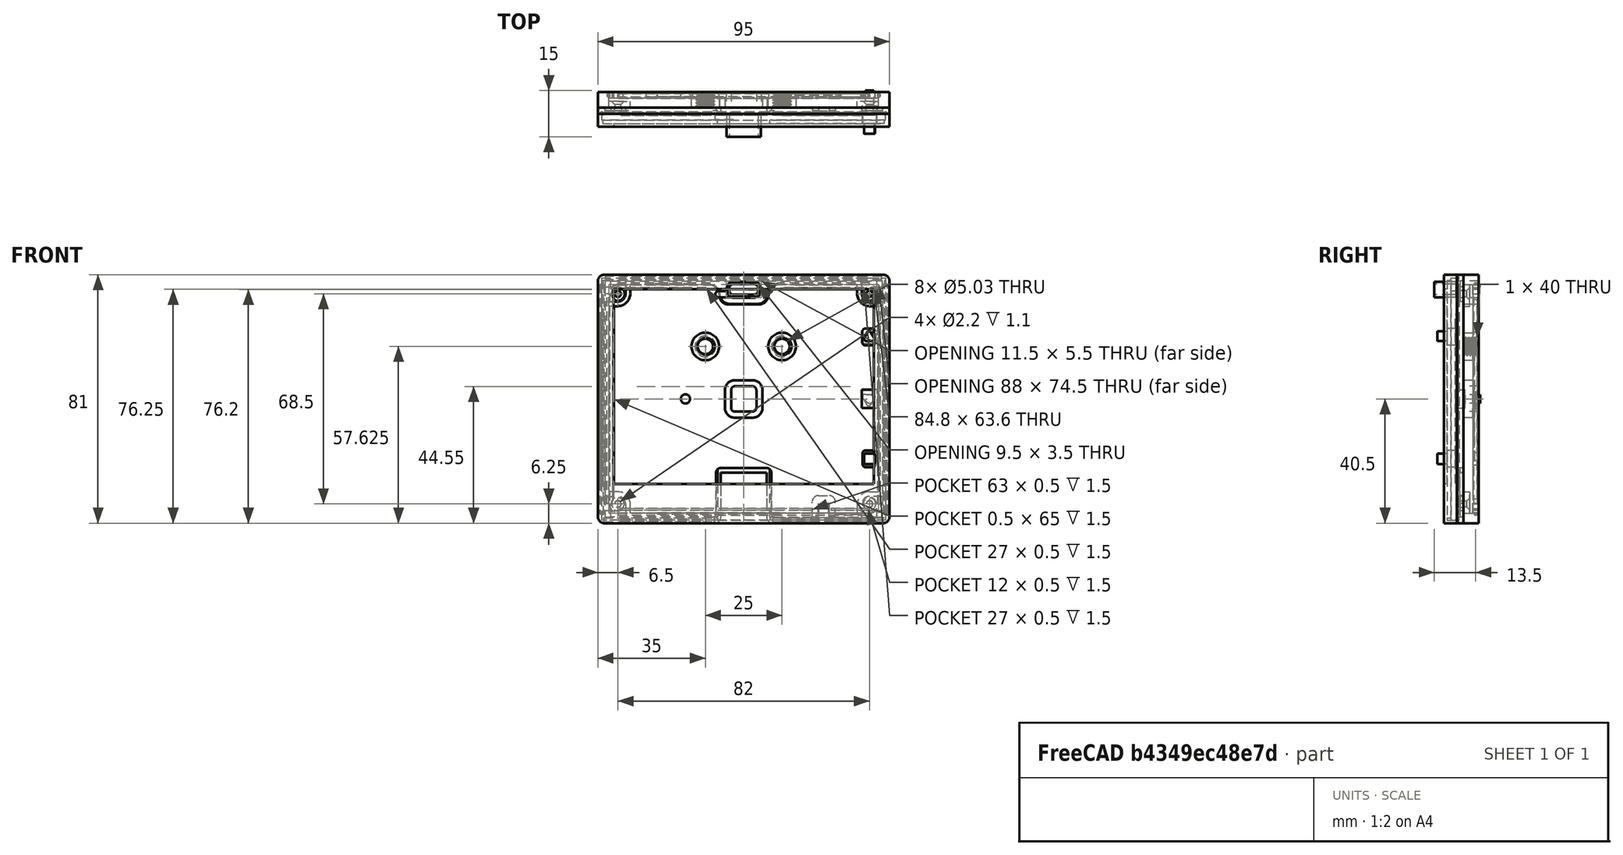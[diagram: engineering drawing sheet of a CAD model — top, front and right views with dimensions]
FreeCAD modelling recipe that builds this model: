
FCSTD DOCUMENT  (FreeCAD 1.1RUnknown)
Label: Altruist_Insight
License: All rights reserved
LicenseURL: http://en.wikipedia.org/wiki/All_rights_reserved
objects: Sketcher::SketchObject×26, PartDesign::Pad×18, PartDesign::Body×8, App::Point×8, PartDesign::Groove×7, PartDesign::Revolution×6, PartDesign::Pocket×4, PartDesign::Mirrored×3, PartDesign::Chamfer×1, Mesh::Feature×1, PartDesign::Hole×1
note: 177 computed .brp shape members not serialized (recipe doc carries the construction recipe); baked Part::Feature solids carry a one-line shape summary decoded from their .brp

FEATURE [Sketcher::SketchObject] Sketch004
  ArcFitTolerance = 1e-06
  AttachmentSupport = -> [XZ_Plane003]
  ExternalTypes = [0]
  FullyConstrained = true
  MakeInternals = false
  MapMode = 5
  Placement = pos=(0,0,0) rot=(1,0,0;1.5708rad)
  _ExternalGeoVersion = 0
  sketch-geometry (14):
    g0: LineSegment StartX=-42.4 StartY=-27.75 StartZ=0 EndX=42.4 EndY=-27.75 EndZ=0
    g1: LineSegment StartX=42.4 StartY=-27.75 StartZ=0 EndX=42.4 EndY=35.85 EndZ=0
    g2: LineSegment StartX=42.4 StartY=35.85 StartZ=0 EndX=-42.4 EndY=35.85 EndZ=0
    g3: LineSegment StartX=-42.4 StartY=35.85 StartZ=0 EndX=-42.4 EndY=-27.75 EndZ=0
    g4: LineSegment StartX=-47.5 StartY=38.5 StartZ=0 EndX=-47.5 EndY=-38.5 EndZ=0
    g5: LineSegment StartX=-45.5 StartY=-40.5 StartZ=0 EndX=45.5 EndY=-40.5 EndZ=0
    g6: LineSegment StartX=47.5 StartY=-38.5 StartZ=0 EndX=47.5 EndY=38.5 EndZ=0
    g7: LineSegment StartX=45.5 StartY=40.5 StartZ=0 EndX=-45.5 EndY=40.5 EndZ=0
    g8: ArcOfCircle CenterX=-45.5 CenterY=38.5 CenterZ=0 NormalX=0 NormalY=0 NormalZ=1 AngleXU=0 Radius=2 StartAngle=1.5708 EndAngle=3.14159
    g9: ArcOfCircle CenterX=-45.5 CenterY=-38.5 CenterZ=0 NormalX=0 NormalY=0 NormalZ=1 AngleXU=0 Radius=2 StartAngle=3.14159 EndAngle=4.71239
    g10: ArcOfCircle CenterX=45.5 CenterY=-38.5 CenterZ=0 NormalX=0 NormalY=0 NormalZ=1 AngleXU=0 Radius=2 StartAngle=4.71239 EndAngle=6.28319
    g11: ArcOfCircle CenterX=45.5 CenterY=38.5 CenterZ=0 NormalX=0 NormalY=0 NormalZ=1 AngleXU=0 Radius=2 StartAngle=-1.8e-15 EndAngle=1.5708
    g12: GeomPoint [constr] X=-47.5 Y=40.5 Z=0
    g13: GeomPoint [constr] X=47.5 Y=-40.5 Z=0
  constraints (34):
    c: Coincident(g0,g1)
    c: Coincident(g1,g2)
    c: Coincident(g2,g3)
    c: Coincident(g3,g0)
    c: Horizontal(g0)
    c: Vertical(g1)
    c: Vertical(g3)
    c: Distance(g1,g3) = 84.8
    c: Distance(g0,g2) = 63.6
    c: Tangent(g4,g8) = -1.5708
    c: Tangent(g4,g9) = -1.5708
    c: Tangent(g5,g9) = -1.5708
    c: Tangent(g5,g10) = -1.5708
    c: Tangent(g6,g10) = -1.5708
    c: Tangent(g6,g11) = -1.5708
    c: Tangent(g7,g11) = -1.5708
    c: Tangent(g7,g8) = -1.5708
    c: Vertical(g4)
    c: Vertical(g6)
    c: Horizontal(g5)
    c: Horizontal(g7)
    c: Equal(g8,g9)
    c: Equal(g9,g10)
    c: Equal(g10,g11)
    c: PointOnObject(g12,g4)
    c: PointOnObject(g12,g7)
    c: PointOnObject(g13,g5)
    c: PointOnObject(g13,g6)
    c: Radius(g9) = 2
    c: Distance(g6,g4) = 95
    c: Distance(g5,g7) = 81
    c: Symmetric(g12,g13,g-1)
    c: Symmetric(g2,g1,g-2)
    c: Distance(g2,g7) = 4.65
FEATURE [PartDesign::Pad] Pad004
  Direction = (0,-1,2e-16)
  Length = 1
  Length2 = 10
  Placement = pos=(0,0,0) rot=(1,0,0;1.5708rad)
  Profile = -> Sketch004
  ReferenceAxis = -> Sketch004 [N_Axis]
  SideType = 0
  Suppressed = false
  Type = 0
  Type2 = 0
FEATURE [Sketcher::SketchObject] Sketch005
  ArcFitTolerance = 1e-06
  AttachmentSupport = -> [Pad004]
  ExternalGeometry = -> [Sketch004]
  ExternalTypes = [0]
  FullyConstrained = true
  MakeInternals = false
  MapMode = 5
  Placement = pos=(0,4e-16,0) rot=(-1,0,0;1.5708rad)
  _ExternalGeoVersion = 0
  sketch-geometry (18):
    g0: LineSegment StartX=45.875 StartY=-38.75 StartZ=0 EndX=45.875 EndY=38.75 EndZ=0
    g1: LineSegment StartX=-45.875 StartY=-38.75 StartZ=0 EndX=-45.875 EndY=38.75 EndZ=0
    g2: LineSegment StartX=-45.875 StartY=38.75 StartZ=0 EndX=-8.5 EndY=38.75 EndZ=0
    g3: LineSegment StartX=45.875 StartY=38.75 StartZ=0 EndX=8.5 EndY=38.75 EndZ=0
    g4: LineSegment StartX=8.5 StartY=38.75 StartZ=0 EndX=8.5 EndY=39.5 EndZ=0
    g5: LineSegment StartX=-8.5 StartY=38.75 StartZ=0 EndX=-8.5 EndY=39.5 EndZ=0
    g6: LineSegment StartX=-8.5 StartY=39.5 StartZ=0 EndX=8.5 EndY=39.5 EndZ=0
    g7: LineSegment StartX=-45.875 StartY=-38.75 StartZ=0 EndX=45.875 EndY=-38.75 EndZ=0
    g8: LineSegment StartX=-47.5 StartY=38.5 StartZ=0 EndX=-47.5 EndY=-38.5 EndZ=0
    g9: LineSegment StartX=-45.5 StartY=-40.5 StartZ=0 EndX=45.5 EndY=-40.5 EndZ=0
    g10: LineSegment StartX=47.5 StartY=-38.5 StartZ=0 EndX=47.5 EndY=38.5 EndZ=0
    g11: LineSegment StartX=45.5 StartY=40.5 StartZ=0 EndX=-45.5 EndY=40.5 EndZ=0
    g12: ArcOfCircle CenterX=-45.5 CenterY=38.5 CenterZ=0 NormalX=0 NormalY=0 NormalZ=1 AngleXU=0 Radius=2 StartAngle=1.5708 EndAngle=3.14159
    g13: ArcOfCircle CenterX=-45.5 CenterY=-38.5 CenterZ=0 NormalX=0 NormalY=0 NormalZ=1 AngleXU=0 Radius=2 StartAngle=3.14159 EndAngle=4.71239
    g14: ArcOfCircle CenterX=45.5 CenterY=-38.5 CenterZ=0 NormalX=0 NormalY=0 NormalZ=1 AngleXU=0 Radius=2 StartAngle=4.71239 EndAngle=6.28319
    g15: ArcOfCircle CenterX=45.5 CenterY=38.5 CenterZ=0 NormalX=0 NormalY=0 NormalZ=1 AngleXU=0 Radius=2 StartAngle=1.3e-15 EndAngle=1.5708
    g16: GeomPoint [constr] X=-47.5 Y=40.5 Z=0
    g17: GeomPoint [constr] X=47.5 Y=-40.5 Z=0
  constraints (44):
    c: Vertical(g0)
    c: Vertical(g1)
    c: DistanceX(g1,g0) = 91.75
    c: DistanceY(g1,g1) = 77.5
    c: Symmetric(g0,g1,g-1)
    c: Coincident(g2,g1)
    c: Horizontal(g2)
    c: Coincident(g3,g0)
    c: Horizontal(g3)
    c: Coincident(g4,g3)
    c: Vertical(g4)
    c: Coincident(g5,g2)
    c: Vertical(g5)
    c: Coincident(g6,g5)
    c: Coincident(g6,g4)
    c: Symmetric(g5,g4,g-2)
    c: Equal(g0,g1)
    c: DistanceX(g6,g6) = 17
    c: Coincident(g7,g1)
    c: Coincident(g7,g0)
    c: Horizontal(g7)
    c: Distance(g4,g4) = 0.75
    c: Tangent(g8,g12) = -1.5708
    c: Tangent(g8,g13) = -1.5708
    c: Tangent(g9,g13) = -1.5708
    c: Tangent(g9,g14) = -1.5708
    c: Tangent(g10,g14) = -1.5708
    c: Tangent(g10,g15) = -1.5708
    c: Tangent(g11,g15) = -1.5708
    c: Tangent(g11,g12) = -1.5708
    c: Vertical(g8)
    c: Vertical(g10)
    c: Horizontal(g9)
    c: Horizontal(g11)
    c: Equal(g12,g13)
    c: Equal(g13,g14)
    c: Equal(g14,g15)
    c: PointOnObject(g16,g8)
    c: PointOnObject(g16,g11)
    c: PointOnObject(g17,g9)
    c: PointOnObject(g17,g10)
    c: Radius(g13) = 2
    c: Symmetric(g15,g13,g-1)
    c: Coincident(g-3,g11)
FEATURE [PartDesign::Pad] Pad005
  BaseFeature = -> Pad004
  Direction = (0,1,2e-16)
  Length = 1.2
  Length2 = 10
  Placement = pos=(0,0,0) rot=(1,0,0;1.5708rad)
  Profile = -> Sketch005
  ReferenceAxis = -> Sketch005 [N_Axis]
  Refine = true
  SideType = 0
  Suppressed = false
  Type = 0
  Type2 = 0
FEATURE [Sketcher::SketchObject] Sketch006
  ArcFitTolerance = 1e-06
  AttachmentSupport = -> [Pad005]
  ExternalGeometry = -> [Pad005]
  ExternalTypes = [0]
  FullyConstrained = true
  MakeInternals = false
  MapMode = 5
  Placement = pos=(0,1.2,0) rot=(-1,0,0;1.5708rad)
  _ExternalGeoVersion = 0
  sketch-geometry (14):
    g0: LineSegment StartX=-46.25 StartY=39.5 StartZ=0 EndX=-46.25 EndY=-39.5 EndZ=0
    g1: LineSegment StartX=-46.25 StartY=-39.5 StartZ=0 EndX=46.25 EndY=-39.5 EndZ=0
    g2: LineSegment StartX=46.25 StartY=-39.5 StartZ=0 EndX=46.25 EndY=39.5 EndZ=0
    g3: LineSegment StartX=46.25 StartY=39.5 StartZ=0 EndX=-46.25 EndY=39.5 EndZ=0
    g4: LineSegment StartX=-47.5 StartY=38.5 StartZ=0 EndX=-47.5 EndY=-38.5 EndZ=0
    g5: LineSegment StartX=-45.5 StartY=-40.5 StartZ=0 EndX=45.5 EndY=-40.5 EndZ=0
    g6: LineSegment StartX=47.5 StartY=-38.5 StartZ=0 EndX=47.5 EndY=38.5 EndZ=0
    g7: LineSegment StartX=45.5 StartY=40.5 StartZ=0 EndX=-45.5 EndY=40.5 EndZ=0
    g8: ArcOfCircle CenterX=-45.5 CenterY=38.5 CenterZ=0 NormalX=0 NormalY=0 NormalZ=1 AngleXU=0 Radius=2 StartAngle=1.5708 EndAngle=3.14159
    g9: ArcOfCircle CenterX=-45.5 CenterY=-38.5 CenterZ=0 NormalX=0 NormalY=0 NormalZ=1 AngleXU=0 Radius=2 StartAngle=3.14159 EndAngle=4.71239
    g10: ArcOfCircle CenterX=45.5 CenterY=-38.5 CenterZ=0 NormalX=0 NormalY=0 NormalZ=1 AngleXU=0 Radius=2 StartAngle=4.71239 EndAngle=6.28319
    g11: ArcOfCircle CenterX=45.5 CenterY=38.5 CenterZ=0 NormalX=0 NormalY=0 NormalZ=1 AngleXU=0 Radius=2 StartAngle=1.6e-15 EndAngle=1.5708
    g12: GeomPoint [constr] X=-47.5 Y=40.5 Z=0
    g13: GeomPoint [constr] X=47.5 Y=-40.5 Z=0
  constraints (33):
    c: Coincident(g0,g1)
    c: Coincident(g1,g2)
    c: Coincident(g2,g3)
    c: Coincident(g3,g0)
    c: Vertical(g0)
    c: Vertical(g2)
    c: Horizontal(g1)
    c: Horizontal(g3)
    c: DistanceY(g2,g2) = 79
    c: DistanceX(g3,g3) = 92.5
    c: Symmetric(g0,g2,g-1)
    c: Tangent(g4,g8) = -1.5708
    c: Tangent(g4,g9) = -1.5708
    c: Tangent(g5,g9) = -1.5708
    c: Tangent(g5,g10) = -1.5708
    c: Tangent(g6,g10) = -1.5708
    c: Tangent(g6,g11) = -1.5708
    c: Tangent(g7,g11) = -1.5708
    c: Tangent(g7,g8) = -1.5708
    c: Vertical(g4)
    c: Vertical(g6)
    c: Horizontal(g5)
    c: Horizontal(g7)
    c: Equal(g8,g9)
    c: Equal(g9,g10)
    c: Equal(g10,g11)
    c: PointOnObject(g12,g4)
    c: PointOnObject(g12,g7)
    c: PointOnObject(g13,g5)
    c: PointOnObject(g13,g6)
    c: Radius(g9) = 2
    c: Symmetric(g11,g9,g-1)
    c: Coincident(g-3,g7)
FEATURE [PartDesign::Pad] Pad006
  BaseFeature = -> Pad005
  Direction = (0,1,2e-16)
  Length = 2
  Length2 = 10
  Placement = pos=(0,0,0) rot=(1,0,0;1.5708rad)
  Profile = -> Sketch006
  ReferenceAxis = -> Sketch006 [N_Axis]
  Refine = true
  SideType = 0
  Suppressed = false
  Type = 0
  Type2 = 0
FEATURE [Sketcher::SketchObject] Sketch007
  ArcFitTolerance = 1e-06
  AttachmentSupport = -> [Pad006]
  ExternalTypes = [0]
  FullyConstrained = true
  MakeInternals = false
  MapMode = 5
  Placement = pos=(0,0,39.5) rot=(1,0,0;3.14159rad)
  _ExternalGeoVersion = 0
  sketch-geometry (4):
    g0: LineSegment StartX=40 StartY=-3.2 StartZ=0 EndX=40 EndY=-2.7 EndZ=0
    g1: LineSegment StartX=40 StartY=-2.7 StartZ=0 EndX=-40 EndY=-2.7 EndZ=0
    g2: LineSegment StartX=-40 StartY=-2.7 StartZ=0 EndX=-40 EndY=-3.2 EndZ=0
    g3: LineSegment StartX=-40 StartY=-3.2 StartZ=0 EndX=40 EndY=-3.2 EndZ=0
  constraints (11):
    c: Coincident(g0,g1)
    c: Coincident(g1,g2)
    c: Coincident(g2,g3)
    c: Coincident(g3,g0)
    c: Vertical(g0)
    c: Vertical(g2)
    c: DistanceY(g2,g2) = 0.5
    c: Symmetric(g1,g0,g-2)
    c: DistanceX(g1,g1) = 80
    c: Distance(g-1,g3) = 3.2
    c: Horizontal(g3)
FEATURE [PartDesign::Revolution] Revolution
  Angle = 360
  Angle2 = 60
  Axis = (1,0,0)
  Base = (-46.25,3.2,39.5)
  BaseFeature = -> Pad006
  FuseOrder = 1
  Placement = pos=(0,0,0) rot=(1,0,0;1.5708rad)
  Profile = -> Sketch007
  ReferenceAxis = -> Pad006 [Edge26]
  Refine = true
  Suppressed = false
  Type = 0
FEATURE [Sketcher::SketchObject] Sketch008
  ArcFitTolerance = 1e-06
  AttachmentSupport = -> [Revolution]
  ExternalTypes = [0]
  FullyConstrained = true
  MakeInternals = false
  MapMode = 5
  Placement = pos=(46.25,0,0) rot=(0.707107,0,-0.707107;3.14159rad)
  _ExternalGeoVersion = 0
  sketch-geometry (4):
    g0: LineSegment StartX=-27.5 StartY=-2.7 StartZ=0 EndX=-27.5 EndY=-3.2 EndZ=0
    g1: LineSegment StartX=-27.5 StartY=-3.2 StartZ=0 EndX=27.5 EndY=-3.2 EndZ=0
    g2: LineSegment StartX=27.5 StartY=-3.2 StartZ=0 EndX=27.5 EndY=-2.7 EndZ=0
    g3: LineSegment StartX=27.5 StartY=-2.7 StartZ=0 EndX=-27.5 EndY=-2.7 EndZ=0
  constraints (11):
    c: Coincident(g0,g1)
    c: Coincident(g1,g2)
    c: Coincident(g2,g3)
    c: Coincident(g3,g0)
    c: Vertical(g0)
    c: Vertical(g2)
    c: Horizontal(g1)
    c: Horizontal(g0,g-3)
    c: Equal(g0,g-3)
    c: Symmetric(g2,g0,g-2)
    c: DistanceX(g3,g3) = 55
FEATURE [PartDesign::Revolution] Revolution001
  Angle = 360
  Angle2 = 60
  Axis = (0,2e-16,-1)
  Base = (46.25,3.2,39.5)
  BaseFeature = -> Revolution
  FuseOrder = 1
  Placement = pos=(0,0,0) rot=(1,0,0;1.5708rad)
  Profile = -> Sketch008
  ReferenceAxis = -> Revolution [Edge19]
  Refine = true
  Reversed = true
  Suppressed = false
  Type = 0
FEATURE [Sketcher::SketchObject] Sketch011
  ArcFitTolerance = 1e-06
  AttachmentSupport = -> [XZ_Plane004]
  ExternalTypes = [0]
  FullyConstrained = true
  MakeInternals = false
  MapMode = 5
  Placement = pos=(0,0,0) rot=(1,0,0;1.5708rad)
  _ExternalGeoVersion = 0
  sketch-geometry (58):
    g0: LineSegment StartX=-47.5 StartY=38.5 StartZ=0 EndX=-47.5 EndY=-38.5 EndZ=0
    g1: LineSegment StartX=-45.5 StartY=-40.5 StartZ=0 EndX=45.5 EndY=-40.5 EndZ=0
    g2: LineSegment StartX=47.5 StartY=-38.5 StartZ=0 EndX=47.5 EndY=38.5 EndZ=0
    g3: LineSegment StartX=45.5 StartY=40.5 StartZ=0 EndX=-45.5 EndY=40.5 EndZ=0
    g4: ArcOfCircle CenterX=-45.5 CenterY=38.5 CenterZ=0 NormalX=0 NormalY=0 NormalZ=1 AngleXU=0 Radius=2 StartAngle=1.5708 EndAngle=3.14159
    g5: ArcOfCircle CenterX=-45.5 CenterY=-38.5 CenterZ=0 NormalX=0 NormalY=0 NormalZ=1 AngleXU=0 Radius=2 StartAngle=3.14159 EndAngle=4.71239
    g6: ArcOfCircle CenterX=45.5 CenterY=-38.5 CenterZ=0 NormalX=0 NormalY=0 NormalZ=1 AngleXU=0 Radius=2 StartAngle=4.71239 EndAngle=6.28319
    g7: ArcOfCircle CenterX=45.5 CenterY=38.5 CenterZ=0 NormalX=0 NormalY=0 NormalZ=1 AngleXU=0 Radius=2 StartAngle=1e-16 EndAngle=1.5708
    g8: GeomPoint [constr] X=-47.5 Y=40.5 Z=0
    g9: GeomPoint [constr] X=47.5 Y=-40.5 Z=0
    g10: LineSegment StartX=-4.75 StartY=36 StartZ=0 EndX=-4.75 EndY=35.5 EndZ=0
    g11: LineSegment StartX=-3.25 StartY=34 StartZ=0 EndX=3.25 EndY=34 EndZ=0
    g12: LineSegment StartX=4.75 StartY=35.5 StartZ=0 EndX=4.75 EndY=36 EndZ=0
    g13: LineSegment StartX=3.25 StartY=37.5 StartZ=0 EndX=-3.25 EndY=37.5 EndZ=0
    g14: ArcOfCircle CenterX=-3.25 CenterY=36 CenterZ=0 NormalX=0 NormalY=0 NormalZ=1 AngleXU=0 Radius=1.5 StartAngle=1.5708 EndAngle=3.14159
    g15: ArcOfCircle CenterX=-3.25 CenterY=35.5 CenterZ=0 NormalX=0 NormalY=0 NormalZ=1 AngleXU=0 Radius=1.5 StartAngle=3.14159 EndAngle=4.71239
    g16: ArcOfCircle CenterX=3.25 CenterY=35.5 CenterZ=0 NormalX=0 NormalY=0 NormalZ=1 AngleXU=0 Radius=1.5 StartAngle=4.71239 EndAngle=6.28319
    g17: ArcOfCircle CenterX=3.25 CenterY=36 CenterZ=0 NormalX=0 NormalY=0 NormalZ=1 AngleXU=0 Radius=1.5 StartAngle=3e-16 EndAngle=1.5708
    g18: GeomPoint [constr] X=-4.75 Y=37.5 Z=0
    g19: GeomPoint [constr] X=4.75 Y=34 Z=0
    g20: Circle CenterX=41 CenterY=34.25 CenterZ=0 NormalX=0 NormalY=0 NormalZ=1 AngleXU=0 Radius=1
    g21: Circle CenterX=-41 CenterY=34.25 CenterZ=0 NormalX=0 NormalY=0 NormalZ=1 AngleXU=0 Radius=1
    g22: Circle CenterX=-41 CenterY=-34.25 CenterZ=0 NormalX=0 NormalY=0 NormalZ=1 AngleXU=0 Radius=1
    g23: Circle CenterX=41 CenterY=-34.25 CenterZ=0 NormalX=0 NormalY=0 NormalZ=1 AngleXU=0 Radius=1
    g24: ArcOfCircle CenterX=41 CenterY=34.25 CenterZ=0 NormalX=0 NormalY=0 NormalZ=1 AngleXU=0 Radius=3 StartAngle=1e-15 EndAngle=1.5708
    g25: ArcOfCircle CenterX=41 CenterY=-34.25 CenterZ=0 NormalX=0 NormalY=0 NormalZ=1 AngleXU=0 Radius=3 StartAngle=4.71239 EndAngle=6.28319
    g26: ArcOfCircle CenterX=-41 CenterY=-34.25 CenterZ=0 NormalX=0 NormalY=0 NormalZ=1 AngleXU=0 Radius=3 StartAngle=3.14159 EndAngle=4.71239
    g27: ArcOfCircle CenterX=-41 CenterY=-34.25 CenterZ=0 NormalX=0 NormalY=0 NormalZ=1 AngleXU=0 Radius=4 StartAngle=0 EndAngle=1.5708
    g28: ArcOfCircle CenterX=41 CenterY=-34.25 CenterZ=0 NormalX=0 NormalY=0 NormalZ=1 AngleXU=0 Radius=4 StartAngle=1.5708 EndAngle=3.14159
    g29: ArcOfCircle CenterX=41 CenterY=34.25 CenterZ=0 NormalX=0 NormalY=0 NormalZ=1 AngleXU=0 Radius=4 StartAngle=3.14159 EndAngle=4.71239
    g30: ArcOfCircle CenterX=-41 CenterY=34.25 CenterZ=0 NormalX=0 NormalY=0 NormalZ=1 AngleXU=0 Radius=4 StartAngle=4.71239 EndAngle=6.28319
    g31: ArcOfCircle CenterX=-41 CenterY=34.25 CenterZ=0 NormalX=0 NormalY=0 NormalZ=1 AngleXU=0 Radius=3 StartAngle=1.5708 EndAngle=3.14159
    g32: LineSegment StartX=-41 StartY=30.25 StartZ=0 EndX=-44 EndY=30.25 EndZ=0
    g33: LineSegment StartX=-37 StartY=34.25 StartZ=0 EndX=-37 EndY=37.25 EndZ=0
    g34: LineSegment StartX=-41 StartY=37.25 StartZ=0 EndX=-37 EndY=37.25 EndZ=0
    g35: LineSegment StartX=-44 StartY=30.25 StartZ=0 EndX=-44 EndY=34.25 EndZ=0
    g36: LineSegment StartX=-41 StartY=-30.25 StartZ=0 EndX=-44 EndY=-30.25 EndZ=0
    g37: LineSegment StartX=-44 StartY=-30.25 StartZ=0 EndX=-44 EndY=-34.25 EndZ=0
    g38: LineSegment StartX=-41 StartY=-37.25 StartZ=0 EndX=-37 EndY=-37.25 EndZ=0
    g39: LineSegment StartX=-37 StartY=-37.25 StartZ=0 EndX=-37 EndY=-34.25 EndZ=0
    g40: LineSegment StartX=-44 StartY=30.25 StartZ=0 EndX=-44 EndY=-30.25 EndZ=0
    g41: LineSegment StartX=41 StartY=-30.25 StartZ=0 EndX=44 EndY=-30.25 EndZ=0
    g42: LineSegment StartX=44 StartY=-34.25 StartZ=0 EndX=44 EndY=-30.25 EndZ=0
    g43: LineSegment StartX=37 StartY=-34.25 StartZ=0 EndX=37 EndY=-37.25 EndZ=0
    g44: LineSegment StartX=41 StartY=-37.25 StartZ=0 EndX=37 EndY=-37.25 EndZ=0
    g45: LineSegment StartX=-37 StartY=-37.25 StartZ=0 EndX=37 EndY=-37.25 EndZ=0
    g46: LineSegment StartX=44 StartY=34.25 StartZ=0 EndX=44 EndY=30.25 EndZ=0
    g47: LineSegment StartX=37 StartY=34.25 StartZ=0 EndX=37 EndY=37.25 EndZ=0
    g48: LineSegment StartX=37 StartY=37.25 StartZ=0 EndX=41 EndY=37.25 EndZ=0
    g49: LineSegment StartX=41 StartY=30.25 StartZ=0 EndX=44 EndY=30.25 EndZ=0
    g50: LineSegment StartX=44 StartY=-30.25 StartZ=0 EndX=44 EndY=30.25 EndZ=0
    g51: LineSegment StartX=-37 StartY=37.25 StartZ=0 EndX=-10.875 EndY=37.25 EndZ=0
    g52: LineSegment StartX=37 StartY=37.25 StartZ=0 EndX=10.875 EndY=37.25 EndZ=0
    g53: ArcOfCircle CenterX=10.875 CenterY=34.125 CenterZ=0 NormalX=0 NormalY=0 NormalZ=1 AngleXU=0 Radius=3.125 StartAngle=1.5708 EndAngle=3.14159
    g54: ArcOfCircle CenterX=-10.875 CenterY=34.125 CenterZ=0 NormalX=0 NormalY=0 NormalZ=1 AngleXU=0 Radius=3.125 StartAngle=0 EndAngle=1.5708
    g55: ArcOfCircle CenterX=-4.625 CenterY=34.125 CenterZ=0 NormalX=0 NormalY=0 NormalZ=1 AngleXU=0 Radius=3.125 StartAngle=3.14159 EndAngle=4.71239
    g56: ArcOfCircle CenterX=4.625 CenterY=34.125 CenterZ=0 NormalX=0 NormalY=0 NormalZ=1 AngleXU=0 Radius=3.125 StartAngle=4.71239 EndAngle=6.28319
    g57: LineSegment StartX=-4.625 StartY=31 StartZ=0 EndX=4.625 EndY=31 EndZ=0
  constraints (158):
    c: Tangent(g0,g4) = -1.5708
    c: Tangent(g0,g5) = -1.5708
    c: Tangent(g1,g5) = -1.5708
    c: Tangent(g1,g6) = -1.5708
    c: Tangent(g2,g6) = -1.5708
    c: Tangent(g2,g7) = -1.5708
    c: Tangent(g3,g7) = -1.5708
    c: Tangent(g3,g4) = -1.5708
    c: Vertical(g0)
    c: Vertical(g2)
    c: Horizontal(g1)
    c: Horizontal(g3)
    c: Equal(g4,g5)
    c: Equal(g5,g6)
    c: Equal(g6,g7)
    c: PointOnObject(g8,g0)
    c: PointOnObject(g8,g3)
    c: PointOnObject(g9,g1)
    c: PointOnObject(g9,g2)
    c: Distance(g2,g0) = 95
    c: Distance(g1,g3) = 81
    c: Symmetric(g8,g9,g-1)
    c: Tangent(g10,g14) = -1.5708
    c: Tangent(g10,g15) = -1.5708
    c: Tangent(g11,g15) = -1.5708
    c: Tangent(g11,g16) = -1.5708
    c: Tangent(g12,g16) = -1.5708
    c: Tangent(g12,g17) = -1.5708
    c: Tangent(g13,g17) = -1.5708
    c: Tangent(g13,g14) = -1.5708
    c: Vertical(g10)
    c: Vertical(g12)
    c: Horizontal(g11)
    c: Equal(g14,g15)
    c: Equal(g15,g16)
    c: Equal(g16,g17)
    c: PointOnObject(g18,g10)
    c: PointOnObject(g18,g13)
    c: PointOnObject(g19,g11)
    c: PointOnObject(g19,g12)
    c: Radius(g15) = 1.5
    c: Distance(g12,g10) = 9.5
    c: Distance(g11,g13) = 3.5
    c: Symmetric(g13,g13,g-2)
    c: Distance(g-1,g11) = 34
    c: Diameter(g20) = 2
    c: Diameter(g21) = 2
    c: Diameter(g22) = 2
    c: Diameter(g23) = 2
    c: Horizontal(g23,g22)
    c: Horizontal(g20,g21)
    c: Vertical(g20,g23)
    c: Vertical(g21,g22)
    c: Symmetric(g22,g20,g-1)
    c: DistanceX(g21,g20) = 82
    c: Distance(g23,g20) = 68.5
    c: Coincident(g24,g20)
    c: Coincident(g25,g23)
    c: Radius(g26) = 3
    c: Coincident(g26,g22)
    c: Coincident(g27,g22)
    c: Coincident(g28,g23)
    c: Coincident(g29,g20)
    c: Radius(g30) = 4
    c: Coincident(g30,g21)
    c: Equal(g27,g28)
    c: Equal(g28,g29)
    c: Equal(g29,g30)
    c: Coincident(g31,g21)
    c: Equal(g31,g26)
    c: Equal(g26,g25)
    c: Equal(g25,g24)
    c: Coincident(g32,g30)
    c: Horizontal(g32)
    c: Coincident(g33,g30)
    c: Vertical(g33)
    c: Coincident(g34,g31)
    c: Coincident(g34,g33)
    c: Horizontal(g34)
    c: Coincident(g35,g32)
    c: Coincident(g35,g31)
    c: Coincident(g36,g27)
    c: Horizontal(g36)
    c: Coincident(g37,g36)
    c: Coincident(g37,g26)
    c: Coincident(g38,g26)
    c: Coincident(g39,g38)
    c: Coincident(g39,g27)
    c: Vertical(g39)
    c: Coincident(g40,g32)
    c: Coincident(g40,g36)
    c: Vertical(g40)
    c: Coincident(g41,g28)
    c: Horizontal(g41)
    c: Coincident(g42,g25)
    c: Coincident(g42,g41)
    c: Coincident(g43,g28)
    c: Vertical(g43)
    c: Coincident(g44,g25)
    c: Coincident(g44,g43)
    c: Coincident(g45,g38)
    c: Coincident(g45,g43)
    c: Horizontal(g45)
    c: Coincident(g46,g24)
    c: Vertical(g46)
    c: Coincident(g47,g29)
    c: Vertical(g47)
    c: Coincident(g48,g47)
    c: Coincident(g48,g24)
    c: Horizontal(g48)
    c: Coincident(g49,g46)
    c: Horizontal(g49)
    c: Coincident(g50,g41)
    c: Coincident(g50,g46)
    c: Vertical(g50)
    c: Coincident(g51,g33)
    c: Horizontal(g51)
    c: Coincident(g52,g47)
    c: Horizontal(g52)
    c: Coincident(g53,g52)
    c: Coincident(g54,g51)
    c: Vertical(g54,g51)
    c: Horizontal(g54,g54)
    c: Coincident(g55,g54)
    c: Coincident(g56,g53)
    c: Vertical(g56,g56)
    c: Horizontal(g56,g53)
    c: Equal(g56,g53)
    c: Horizontal(g53,g53)
    c: Vertical(g52,g53)
    c: Horizontal(g54,g55)
    c: Vertical(g55,g55)
    c: Equal(g54,g55)
    c: Coincident(g57,g55)
    c: Coincident(g57,g56)
    c: Distance(g11,g57) = 3
    c: Symmetric(g55,g56,g-2)
    c: DistanceX(g12,g53) = 3
    c: Horizontal(g30,g21)
    c: Vertical(g30,g21)
    c: Vertical(g31,g21)
    c: Horizontal(g29,g24)
    c: Vertical(g24,g29)
    c: Horizontal(g24,g20)
    c: Vertical(g49,g20)
    c: Coincident(g49,g29)
    c: Horizontal(g31,g30)
    c: Vertical(g35)
    c: Vertical(g28,g23)
    c: Horizontal(g23,g28)
    c: Vertical(g25,g23)
    c: Horizontal(g44)
    c: Horizontal(g28,g25)
    c: Horizontal(g27,g22)
    c: Vertical(g22,g27)
    c: Vertical(g26,g27)
    c: Horizontal(g26,g27)
    c: Radius(g6) = 2
FEATURE [Sketcher::SketchObject] Sketch015
  ArcFitTolerance = 1e-06
  AttachmentSupport = -> [XZ_Plane001]
  ExternalTypes = [0]
  FullyConstrained = true
  MakeInternals = false
  MapMode = 5
  Placement = pos=(0,0,0) rot=(1,0,0;1.5708rad)
  _ExternalGeoVersion = 0
  sketch-geometry (75):
    g0: LineSegment StartX=-47.5 StartY=38.5 StartZ=0 EndX=-47.5 EndY=-38.5 EndZ=0
    g1: LineSegment StartX=47.5 StartY=-38.5 StartZ=0 EndX=47.5 EndY=38.5 EndZ=0
    g2: LineSegment StartX=45.5 StartY=40.5 StartZ=0 EndX=-45.5 EndY=40.5 EndZ=0
    g3: ArcOfCircle CenterX=-45.5 CenterY=38.5 CenterZ=0 NormalX=0 NormalY=0 NormalZ=1 AngleXU=0 Radius=2 StartAngle=1.5708 EndAngle=3.14159
    g4: ArcOfCircle CenterX=-45.5 CenterY=-38.5 CenterZ=0 NormalX=0 NormalY=0 NormalZ=1 AngleXU=0 Radius=2 StartAngle=3.14159 EndAngle=4.71239
    g5: ArcOfCircle CenterX=45.5 CenterY=-38.5 CenterZ=0 NormalX=0 NormalY=0 NormalZ=1 AngleXU=0 Radius=2 StartAngle=4.71239 EndAngle=6.28319
    g6: ArcOfCircle CenterX=45.5 CenterY=38.5 CenterZ=0 NormalX=0 NormalY=0 NormalZ=1 AngleXU=0 Radius=2 StartAngle=1.2e-15 EndAngle=1.5708
    g7: GeomPoint [constr] X=-47.5 Y=40.5 Z=0
    g8: GeomPoint [constr] X=47.5 Y=-40.5 Z=0
    g9: Circle CenterX=41 CenterY=34.25 CenterZ=0 NormalX=0 NormalY=0 NormalZ=1 AngleXU=0 Radius=1.1
    g10: Circle CenterX=-41 CenterY=34.25 CenterZ=0 NormalX=0 NormalY=0 NormalZ=1 AngleXU=0 Radius=1.1
    g11: Circle CenterX=-41 CenterY=-34.25 CenterZ=0 NormalX=0 NormalY=0 NormalZ=1 AngleXU=0 Radius=1.1
    g12: Circle CenterX=41 CenterY=-34.25 CenterZ=0 NormalX=0 NormalY=0 NormalZ=1 AngleXU=0 Radius=1.1
    g13: LineSegment [constr] StartX=-46.25 StartY=39.5 StartZ=0 EndX=-46.25 EndY=-39.5 EndZ=0
    g14: LineSegment [constr] StartX=-46.25 StartY=-39.5 StartZ=0 EndX=46.25 EndY=-39.5 EndZ=0
    g15: LineSegment [constr] StartX=46.25 StartY=-39.5 StartZ=0 EndX=46.25 EndY=39.5 EndZ=0
    g16: LineSegment [constr] StartX=46.25 StartY=39.5 StartZ=0 EndX=-46.25 EndY=39.5 EndZ=0
    g17: ArcOfCircle CenterX=-41 CenterY=34.25 CenterZ=0 NormalX=0 NormalY=0 NormalZ=1 AngleXU=0 Radius=2.5 StartAngle=4.71239 EndAngle=6.28319
    g18: LineSegment StartX=-38.5 StartY=38.5 StartZ=0 EndX=-38.5 EndY=34.25 EndZ=0
    g19: LineSegment StartX=-41 StartY=31.75 StartZ=0 EndX=-45.25 EndY=31.75 EndZ=0
    g20: LineSegment StartX=45.25 StartY=31.75 StartZ=0 EndX=45.25 EndY=-31.75 EndZ=0
    g21: ArcOfCircle CenterX=41 CenterY=34.25 CenterZ=0 NormalX=0 NormalY=0 NormalZ=1 AngleXU=0 Radius=2.5 StartAngle=3.14159 EndAngle=4.71239
    g22: LineSegment StartX=38.5 StartY=38.5 StartZ=0 EndX=38.5 EndY=34.25 EndZ=0
    g23: LineSegment StartX=41 StartY=31.75 StartZ=0 EndX=45.25 EndY=31.75 EndZ=0
    g24: LineSegment StartX=7.5 StartY=-22.5 StartZ=0 EndX=-7.5 EndY=-22.5 EndZ=0
    g25: LineSegment StartX=7.5 StartY=-24 StartZ=0 EndX=-7.5 EndY=-24 EndZ=0
    g26: LineSegment StartX=-7.5 StartY=-24 StartZ=0 EndX=-7.5 EndY=-38.5 EndZ=0
    g27: LineSegment StartX=7.5 StartY=-24 StartZ=0 EndX=7.5 EndY=-38.5 EndZ=0
    g28: LineSegment StartX=27.85 StartY=-40.5 StartZ=0 EndX=27.85 EndY=-34 EndZ=0
    g29: LineSegment StartX=27.85 StartY=-34 StartZ=0 EndX=24.35 EndY=-34 EndZ=0
    g30: LineSegment StartX=24.35 StartY=-40.5 StartZ=0 EndX=24.35 EndY=-34 EndZ=0
    g31: LineSegment StartX=45.5 StartY=-40.5 StartZ=0 EndX=27.85 EndY=-40.5 EndZ=0
    g32: ArcOfCircle CenterX=9.5 CenterY=-38.5 CenterZ=0 NormalX=0 NormalY=0 NormalZ=1 AngleXU=0 Radius=2 StartAngle=3.14159 EndAngle=4.71239
    g33: LineSegment StartX=24.35 StartY=-40.5 StartZ=0 EndX=9.5 EndY=-40.5 EndZ=0
    g34: ArcOfCircle CenterX=7.5 CenterY=-24 CenterZ=0 NormalX=0 NormalY=0 NormalZ=1 AngleXU=0 Radius=1.5 StartAngle=0 EndAngle=1.5708
    g35: ArcOfCircle CenterX=10 CenterY=-37.5 CenterZ=0 NormalX=0 NormalY=0 NormalZ=1 AngleXU=0 Radius=1 StartAngle=3.14159 EndAngle=4.71239
    g36: LineSegment StartX=9 StartY=-24 StartZ=0 EndX=9 EndY=-37.5 EndZ=0
    g37: ArcOfCircle CenterX=-9.5 CenterY=-38.5 CenterZ=0 NormalX=0 NormalY=0 NormalZ=1 AngleXU=0 Radius=2 StartAngle=4.71239 EndAngle=6.28319
    g38: LineSegment StartX=-9.5 StartY=-40.5 StartZ=0 EndX=-45.5 EndY=-40.5 EndZ=0
    g39: ArcOfCircle CenterX=-7.5 CenterY=-24 CenterZ=0 NormalX=0 NormalY=0 NormalZ=1 AngleXU=0 Radius=1.5 StartAngle=1.5708 EndAngle=3.14159
    g40: LineSegment StartX=-45.25 StartY=31.75 StartZ=0 EndX=-45.25 EndY=-31.75 EndZ=0
    g41: LineSegment StartX=-45.25 StartY=-31.75 StartZ=0 EndX=-41 EndY=-31.75 EndZ=0
    g42: ArcOfCircle CenterX=-41 CenterY=-34.25 CenterZ=0 NormalX=0 NormalY=0 NormalZ=1 AngleXU=0 Radius=2.5 StartAngle=0 EndAngle=1.5708
    g43: LineSegment StartX=-38.5 StartY=-34.25 StartZ=0 EndX=-38.5 EndY=-37.5 EndZ=0
    g44: ArcOfCircle CenterX=-37.5 CenterY=-37.5 CenterZ=0 NormalX=0 NormalY=0 NormalZ=1 AngleXU=0 Radius=1 StartAngle=3.14159 EndAngle=4.71239
    g45: ArcOfCircle CenterX=-10 CenterY=-37.5 CenterZ=0 NormalX=0 NormalY=0 NormalZ=1 AngleXU=0 Radius=1 StartAngle=4.71239 EndAngle=6.28319
    g46: LineSegment StartX=-10 StartY=-38.5 StartZ=0 EndX=-37.5 EndY=-38.5 EndZ=0
    g47: LineSegment StartX=-9 StartY=-24 StartZ=0 EndX=-9 EndY=-37.5 EndZ=0
    g48: LineSegment StartX=10 StartY=-38.5 StartZ=0 EndX=22.35 EndY=-38.5 EndZ=0
    g49: LineSegment StartX=22.35 StartY=-38.5 StartZ=0 EndX=22.35 EndY=-33.5 EndZ=0
    g50: LineSegment StartX=29.85 StartY=-38.5 StartZ=0 EndX=29.85 EndY=-33.5 EndZ=0
    g51: LineSegment StartX=24.35 StartY=-31.5 StartZ=0 EndX=27.85 EndY=-31.5 EndZ=0
    g52: ArcOfCircle CenterX=27.85 CenterY=-33.5 CenterZ=0 NormalX=0 NormalY=0 NormalZ=1 AngleXU=0 Radius=2 StartAngle=-9e-16 EndAngle=1.5708
    g53: ArcOfCircle CenterX=24.35 CenterY=-33.5 CenterZ=0 NormalX=0 NormalY=0 NormalZ=1 AngleXU=0 Radius=2 StartAngle=1.5708 EndAngle=3.14159
    g54: LineSegment StartX=29.85 StartY=-38.5 StartZ=0 EndX=38.5 EndY=-38.5 EndZ=0
    g55: LineSegment StartX=38.5 StartY=-38.5 StartZ=0 EndX=38.5 EndY=-34.25 EndZ=0
    g56: LineSegment StartX=45.25 StartY=-31.75 StartZ=0 EndX=41 EndY=-31.75 EndZ=0
    g57: ArcOfCircle CenterX=41 CenterY=-34.25 CenterZ=0 NormalX=0 NormalY=0 NormalZ=1 AngleXU=0 Radius=2.5 StartAngle=1.5708 EndAngle=3.14159
    g58: LineSegment StartX=-38.5 StartY=38.5 StartZ=0 EndX=38.5 EndY=38.5 EndZ=0
    g59: LineSegment StartX=-45.25 StartY=38.5 StartZ=0 EndX=-45.25 EndY=36.5 EndZ=0
    g60: LineSegment StartX=-45.25 StartY=36.5 StartZ=0 EndX=-43.25 EndY=36.5 EndZ=0
    g61: LineSegment StartX=-43.25 StartY=36.5 StartZ=0 EndX=-43.25 EndY=38.5 EndZ=0
    g62: LineSegment StartX=-43.25 StartY=38.5 StartZ=0 EndX=-45.25 EndY=38.5 EndZ=0
    g63: LineSegment StartX=-45.25 StartY=-38.5 StartZ=0 EndX=-43.25 EndY=-38.5 EndZ=0
    g64: LineSegment StartX=-43.25 StartY=-38.5 StartZ=0 EndX=-43.25 EndY=-36.5 EndZ=0
    g65: LineSegment StartX=-43.25 StartY=-36.5 StartZ=0 EndX=-45.25 EndY=-36.5 EndZ=0
    g66: LineSegment StartX=-45.25 StartY=-36.5 StartZ=0 EndX=-45.25 EndY=-38.5 EndZ=0
    g67: LineSegment StartX=43.25 StartY=-36.5 StartZ=0 EndX=43.25 EndY=-38.5 EndZ=0
    g68: LineSegment StartX=43.25 StartY=-38.5 StartZ=0 EndX=45.25 EndY=-38.5 EndZ=0
    g69: LineSegment StartX=45.25 StartY=-38.5 StartZ=0 EndX=45.25 EndY=-36.5 EndZ=0
    g70: LineSegment StartX=45.25 StartY=-36.5 StartZ=0 EndX=43.25 EndY=-36.5 EndZ=0
    g71: LineSegment StartX=43.25 StartY=38.5 StartZ=0 EndX=43.25 EndY=36.5 EndZ=0
    g72: LineSegment StartX=43.25 StartY=36.5 StartZ=0 EndX=45.25 EndY=36.5 EndZ=0
    g73: LineSegment StartX=45.25 StartY=36.5 StartZ=0 EndX=45.25 EndY=38.5 EndZ=0
    g74: LineSegment StartX=45.25 StartY=38.5 StartZ=0 EndX=43.25 EndY=38.5 EndZ=0
  constraints (220):
    c: Tangent(g0,g3) = -1.5708
    c: Tangent(g0,g4) = -1.5708
    c: Tangent(g1,g6) = -1.5708
    c: Tangent(g2,g6) = -1.5708
    c: Tangent(g2,g3) = -1.5708
    c: Vertical(g0)
    c: Vertical(g1)
    c: Horizontal(g2)
    c: Equal(g3,g4)
    c: Equal(g4,g5)
    c: PointOnObject(g7,g0)
    c: PointOnObject(g7,g2)
    c: Radius(g4) = 2
    c: Distance(g1,g0) = 95
    c: Distance(g4,g2) = 81
    c: Symmetric(g7,g8,g-1)
    c: Diameter(g11) = 2.2
    c: Horizontal(g12,g11)
    c: Horizontal(g9,g10)
    c: Vertical(g9,g12)
    c: Vertical(g10,g11)
    c: Symmetric(g11,g9,g-1)
    c: DistanceX(g10,g9) = 82
    c: Distance(g12,g9) = 68.5
    c: Coincident(g13,g14)
    c: Coincident(g14,g15)
    c: Coincident(g15,g16)
    c: Coincident(g16,g13)
    c: Vertical(g13)
    c: Vertical(g15)
    c: Horizontal(g14)
    c: Horizontal(g16)
    c: Symmetric(g14,g13,g-1)
    c: DistanceY(g13,g13) = 79
    c: DistanceX(g16,g16) = 92.5
    c: Coincident(g10,g17)
    c: Coincident(g18,g17)
    c: Vertical(g18)
    c: Radius(g17) = 2.5
    c: Horizontal(g10,g17)
    c: Vertical(g17,g10)
    c: Tangent(g19,g17) = 1.5708
    c: Vertical(g20)
    c: Distance(g20,g15) = 1
    c: Coincident(g21,g9)
    c: Radius(g21) = 2.5
    c: Coincident(g22,g21)
    c: Vertical(g22)
    c: Coincident(g23,g21)
    c: Coincident(g23,g20)
    c: Horizontal(g23)
    c: Horizontal(g21,g9)
    c: Vertical(g9,g21)
    c: Horizontal(g24)
    c: Coincident(g26,g25)
    c: Vertical(g26)
    c: Coincident(g27,g25)
    c: Vertical(g27)
    c: Coincident(g29,g28)
    c: Horizontal(g29)
    c: Vertical(g30)
    c: Vertical(g28)
    c: Coincident(g29,g30)
    c: Coincident(g31,g5)
    c: Coincident(g31,g28)
    c: Horizontal(g31)
    c: Coincident(g32,g27)
    c: Vertical(g32,g32)
    c: Horizontal(g27,g32)
    c: Coincident(g33,g30)
    c: Tangent(g33,g32) = 1.5708
    c: Coincident(g34,g25)
    c: Coincident(g34,g24)
    c: Coincident(g36,g34)
    c: Coincident(g36,g35)
    c: Vertical(g36)
    c: Horizontal(g28,g30)
    c: Coincident(g37,g26)
    c: Horizontal(g37,g26)
    c: Vertical(g37,g37)
    c: Coincident(g38,g37)
    c: Coincident(g38,g4)
    c: Horizontal(g38)
    c: Coincident(g39,g25)
    c: Coincident(g39,g24)
    c: Vertical(g24,g25)
    c: Horizontal(g25,g39)
    c: Symmetric(g25,g25,g-2)
    c: DistanceX(g25,g25) = 15
    c: Vertical(g24,g25)
    c: Vertical(g40)
    c: Coincident(g41,g40)
    c: Horizontal(g41)
    c: Coincident(g42,g11)
    c: Coincident(g42,g41)
    c: Vertical(g41,g11)
    c: Horizontal(g42,g11)
    c: Radius(g42) = 2.5
    c: Coincident(g43,g42)
    c: Vertical(g43)
    c: Coincident(g44,g43)
    c: Coincident(g46,g45)
    c: Coincident(g46,g44)
    c: Horizontal(g46)
    c: Coincident(g47,g39)
    c: Vertical(g47)
    c: Radius(g44) = 1
    c: Distance(g14,g46) = 1
    c: Radius(g45) = 1
    c: Coincident(g47,g45)
    c: Horizontal(g45,g45)
    c: Vertical(g45,g45)
    c: Equal(g45,g35)
    c: Equal(g32,g37)
    c: Radius(g39) = 1.5
    c: DistanceY(g26,g26) = 14.5
    c: Horizontal(g34,g25)
    c: Vertical(g35,g35)
    c: Horizontal(g35,g35)
    c: DistanceX(g29,g29) = 3.5
    c: DistanceY(g30,g30) = 6.5
    c: Vertical(g5,g5)
    c: Coincident(g5,g1)
    c: Symmetric(g2,g4,g-1)
    c: Symmetric(g1,g0,g-2)
    c: Equal(g5,g32)
    c: Horizontal(g32,g37)
    c: DistanceX(g33,g33) = 14.85
    c: Horizontal(g5,g1)
    c: Horizontal(g44,g43)
    c: Vertical(g44,g44)
    c: Tangent(g48,g35) = -1.5708
    c: Coincident(g49,g48)
    c: Vertical(g49)
    c: Vertical(g50)
    c: Horizontal(g51)
    c: Coincident(g52,g51)
    c: Coincident(g52,g50)
    c: Coincident(g53,g49)
    c: Coincident(g53,g51)
    c: Horizontal(g53,g49)
    c: Equal(g53,g32)
    c: Equal(g52,g53)
    c: Vertical(g53,g51)
    c: Vertical(g52,g51)
    c: Horizontal(g52,g50)
    c: Coincident(g54,g50)
    c: Horizontal(g54)
    c: Horizontal(g48,g50)
    c: Horizontal(g45,g35)
    c: Coincident(g55,g54)
    c: Vertical(g55)
    c: Coincident(g56,g20)
    c: Horizontal(g56)
    c: Distance(g29,g51) = 2.5
    c: Vertical(g51,g29)
    c: Equal(g51,g29)
    c: Coincident(g57,g55)
    c: Coincident(g57,g56)
    c: Coincident(g12,g57)
    c: Equal(g57,g21)
    c: Vertical(g56,g12)
    c: Horizontal(g55,g12)
    c: Coincident(g58,g18)
    c: Horizontal(g58)
    c: Distance(g18,g16) = 1
    c: Distance(g40,g13) = 1
    c: Coincident(g19,g40)
    c: Equal(g12,g11)
    c: Equal(g9,g11)
    c: Equal(g10,g11)
    c: Coincident(g59,g60)
    c: Coincident(g60,g61)
    c: Coincident(g61,g62)
    c: Coincident(g62,g59)
    c: Vertical(g59)
    c: Vertical(g61)
    c: Horizontal(g60)
    c: Horizontal(g62)
    c: Distance(g59,g61) = 2
    c: Equal(g59,g62)
    c: Vertical(g19,g59)
    c: Horizontal(g61,g18)
    c: Coincident(g63,g64)
    c: Coincident(g64,g65)
    c: Coincident(g65,g66)
    c: Coincident(g66,g63)
    c: Horizontal(g63)
    c: Horizontal(g65)
    c: Vertical(g64)
    c: Vertical(g66)
    c: Equal(g65,g66)
    c: Equal(g65,g62)
    c: Vertical(g65,g40)
    c: Horizontal(g63,g44)
    c: Coincident(g67,g68)
    c: Coincident(g68,g69)
    c: Coincident(g69,g70)
    c: Coincident(g70,g67)
    c: Vertical(g67)
    c: Vertical(g69)
    c: Horizontal(g68)
    c: Horizontal(g70)
    c: Equal(g70,g67)
    c: Equal(g70,g62)
    c: Horizontal(g54,g67)
    c: Vertical(g20,g69)
    c: Coincident(g22,g58)
    c: Coincident(g71,g72)
    c: Coincident(g72,g73)
    c: Coincident(g73,g74)
    c: Coincident(g74,g71)
    c: Vertical(g71)
    c: Vertical(g73)
    c: Horizontal(g72)
    c: Horizontal(g74)
    c: Equal(g71,g74)
    c: Equal(g74,g62)
    c: Horizontal(g71,g22)
    c: Vertical(g72,g20)
FEATURE [PartDesign::Pad] Pad008
  Direction = (0,-1,2e-16)
  Length = 2
  Length2 = 10
  Placement = pos=(0,0,0) rot=(1,0,0;1.5708rad)
  Profile = -> Sketch015
  ReferenceAxis = -> Sketch015 [N_Axis]
  Refine = true
  SideType = 0
  Suppressed = false
  Type = 0
  Type2 = 0
FEATURE [Sketcher::SketchObject] Sketch016
  ArcFitTolerance = 1e-06
  AttachmentSupport = -> [Pad008]
  ExternalGeometry = -> [Pad008]
  ExternalTypes = [0]
  FullyConstrained = true
  MakeInternals = false
  MapMode = 5
  Placement = pos=(0,-2,0) rot=(1,0,0;1.5708rad)
  _ExternalGeoVersion = 0
  sketch-geometry (20):
    g0: LineSegment StartX=9.5 StartY=-39.4 StartZ=0 EndX=9.5 EndY=-40 EndZ=0
    g1: LineSegment StartX=9.5 StartY=-40 StartZ=0 EndX=45.5 EndY=-40 EndZ=0
    g2: LineSegment StartX=45.5 StartY=-40 StartZ=0 EndX=45.5 EndY=-39.4 EndZ=0
    g3: LineSegment StartX=45.5 StartY=-39.4 StartZ=0 EndX=9.5 EndY=-39.4 EndZ=0
    g4: LineSegment StartX=46.25 StartY=-37.5 StartZ=0 EndX=46.85 EndY=-37.5 EndZ=0
    g5: LineSegment StartX=46.85 StartY=-37.5 StartZ=0 EndX=46.85 EndY=37.5 EndZ=0
    g6: LineSegment StartX=46.85 StartY=37.5 StartZ=0 EndX=46.25 EndY=37.5 EndZ=0
    g7: LineSegment StartX=46.25 StartY=37.5 StartZ=0 EndX=46.25 EndY=-37.5 EndZ=0
    g8: LineSegment StartX=45 StartY=39.4 StartZ=0 EndX=45 EndY=40 EndZ=0
    g9: LineSegment StartX=45 StartY=40 StartZ=0 EndX=-45 EndY=40 EndZ=0
    g10: LineSegment StartX=-45 StartY=40 StartZ=0 EndX=-45 EndY=39.4 EndZ=0
    g11: LineSegment StartX=-45 StartY=39.4 StartZ=0 EndX=45 EndY=39.4 EndZ=0
    g12: LineSegment StartX=-46.25 StartY=37.5 StartZ=0 EndX=-46.85 EndY=37.5 EndZ=0
    g13: LineSegment StartX=-46.85 StartY=37.5 StartZ=0 EndX=-46.85 EndY=-37.5 EndZ=0
    g14: LineSegment StartX=-46.85 StartY=-37.5 StartZ=0 EndX=-46.25 EndY=-37.5 EndZ=0
    g15: LineSegment StartX=-46.25 StartY=-37.5 StartZ=0 EndX=-46.25 EndY=37.5 EndZ=0
    g16: LineSegment StartX=-45.5 StartY=-39.4 StartZ=0 EndX=-45.5 EndY=-40 EndZ=0
    g17: LineSegment StartX=-45.5 StartY=-40 StartZ=0 EndX=-9.5 EndY=-40 EndZ=0
    g18: LineSegment StartX=-9.5 StartY=-40 StartZ=0 EndX=-9.5 EndY=-39.4 EndZ=0
    g19: LineSegment StartX=-9.5 StartY=-39.4 StartZ=0 EndX=-45.5 EndY=-39.4 EndZ=0
  constraints (57):
    c: Coincident(g0,g1)
    c: Coincident(g1,g2)
    c: Coincident(g2,g3)
    c: Coincident(g3,g0)
    c: Vertical(g0)
    c: Vertical(g2)
    c: Horizontal(g1)
    c: Horizontal(g3)
    c: Coincident(g4,g5)
    c: Coincident(g5,g6)
    c: Coincident(g6,g7)
    c: Coincident(g7,g4)
    c: Horizontal(g4)
    c: Horizontal(g6)
    c: Vertical(g5)
    c: PointOnObject(g4,g-5)
    c: Coincident(g8,g9)
    c: Coincident(g9,g10)
    c: Coincident(g10,g11)
    c: Coincident(g11,g8)
    c: Vertical(g8)
    c: Vertical(g10)
    c: Horizontal(g9)
    c: Coincident(g12,g13)
    c: Coincident(g13,g14)
    c: Coincident(g14,g15)
    c: Coincident(g15,g12)
    c: Horizontal(g12)
    c: Horizontal(g14)
    c: Vertical(g13)
    c: Vertical(g15)
    c: PointOnObject(g12,g-3)
    c: Symmetric(g10,g8,g-2)
    c: Distance(g8,g8) = 0.6
    c: DistanceX(g9,g9) = 90
    c: Symmetric(g4,g6,g-1)
    c: DistanceY(g5,g5) = 75
    c: Equal(g6,g8)
    c: Equal(g8,g12)
    c: Equal(g12,g0)
    c: Coincident(g16,g17)
    c: Coincident(g17,g18)
    c: Coincident(g18,g19)
    c: Coincident(g19,g16)
    c: Vertical(g16)
    c: Vertical(g18)
    c: Horizontal(g17)
    c: Horizontal(g19)
    c: Equal(g0,g18)
    c: Symmetric(g18,g0,g-2)
    c: Distance(g0,g18) = 19
    c: DistanceX(g1,g1) = 36
    c: Equal(g17,g1)
    c: Horizontal(g6,g12)
    c: Horizontal(g14,g4)
    c: Distance(g9,g-7) = 0.5
    c: Distance(g1,g-8) = 0.5
FEATURE [PartDesign::Groove] Groove
  Angle = 360
  Angle2 = 60
  Axis = (0,2e-16,1)
  Base = (-46.25,-2,-37.5)
  BaseFeature = -> Pad008
  Placement = pos=(0,0,0) rot=(1,0,0;1.5708rad)
  Profile = -> Sketch016 [Edge16,Edge15,Edge14,Edge13]
  ReferenceAxis = -> Sketch016 [Edge16]
  Refine = true
  Reversed = true
  Suppressed = false
  Type = 0
FEATURE [PartDesign::Groove] Groove001
  Angle = 360
  Angle2 = 60
  Axis = (1,0,0)
  Base = (-45,-2,39.4)
  BaseFeature = -> Groove
  Placement = pos=(0,0,0) rot=(1,0,0;1.5708rad)
  Profile = -> Sketch016 [Edge12,Edge11,Edge10,Edge9]
  ReferenceAxis = -> Sketch016 [Edge12]
  Refine = true
  Suppressed = false
  Type = 0
FEATURE [PartDesign::Groove] Groove002
  Angle = 360
  Angle2 = 60
  Axis = (0,-2e-16,-1)
  Base = (46.25,-2,37.5)
  BaseFeature = -> Groove001
  Placement = pos=(0,0,0) rot=(1,0,0;1.5708rad)
  Profile = -> Sketch016 [Edge5,Edge8,Edge6,Edge7]
  ReferenceAxis = -> Sketch016 [Edge8]
  Refine = true
  Suppressed = false
  Type = 0
FEATURE [PartDesign::Groove] Groove003
  Angle = 360
  Angle2 = 60
  Axis = (-1,0,0)
  Base = (45.5,-2,-39.4)
  BaseFeature = -> Groove002
  Placement = pos=(0,0,0) rot=(1,0,0;1.5708rad)
  Profile = -> Sketch016 [Edge18,Edge19,Edge20,Edge17,Edge1,Edge2,Edge4,Edge3]
  ReferenceAxis = -> Sketch016 [Edge4]
  Refine = true
  Reversed = true
  Suppressed = false
  Type = 0
FEATURE [PartDesign::Pad] Pad009
  Direction = (0,-1,2e-16)
  Length = 5
  Length2 = 10
  Placement = pos=(0,0,0) rot=(1,0,0;1.5708rad)
  Profile = -> Sketch011 [Edge3,Edge4,Edge5,Edge6,Edge7,Edge8,Edge1,Edge2,Edge42,Edge40,Edge39,Edge37,Edge38,Edge41,Edge43,Edge47,Edge50,Edge48,Edge49,Edge54,Edge24,Edge25,Edge26,Edge27,Edge28,Edge29,Edge30,Edge31,Edge32,Edge33,Edge11,Edge10,Edge9,Edge16,Edge15,Edge14,Edge13,Edge12]
  ReferenceAxis = -> Sketch011 [N_Axis]
  Refine = true
  Reversed = true
  SideType = 0
  Suppressed = false
  Type = 0
  Type2 = 0
FEATURE [PartDesign::Pad] Pad010
  BaseFeature = -> Pad009
  Direction = (0,-1,2e-16)
  Length = 2
  Length2 = 10
  Placement = pos=(0,0,0) rot=(1,0,0;1.5708rad)
  Profile = -> Sketch011 [Edge24,Edge23,Edge22,Edge21,Edge26,Edge25,Edge17,Edge18,Edge36,Edge39,Edge37,Edge38,Edge34,Edge35,Edge43,Edge42,Edge41,Edge45,Edge44,Edge46,Edge19,Edge48,Edge50,Edge51,Edge52,Edge53,Edge49,Edge20]
  ReferenceAxis = -> Sketch011 [N_Axis]
  Refine = true
  Reversed = true
  SideType = 0
  Suppressed = false
  Type = 0
  Type2 = 0
FEATURE [PartDesign::Chamfer] Chamfer
  Angle = 45
  Base = -> Pad010 [Edge115,Edge121,Edge137,Edge148]
  BaseFeature = -> Pad010
  ChamferType = 0
  FlipDirection = false
  Placement = pos=(0,0,0) rot=(1,0,0;1.5708rad)
  Refine = true
  Size = 1
  Size2 = 1
  SupportTransform = false
  Suppressed = false
  UseAllEdges = false
FEATURE [Sketcher::SketchObject] Sketch017
  ArcFitTolerance = 1e-06
  AttachmentSupport = -> [Chamfer]
  ExternalGeometry = -> [Chamfer]
  ExternalTypes = [0]
  FullyConstrained = true
  MakeInternals = false
  MapMode = 5
  Placement = pos=(0,0,37.25) rot=(1,0,0;3.14159rad)
  _ExternalGeoVersion = 0
  sketch-geometry (8):
    g0: LineSegment StartX=-41 StartY=-3.4 StartZ=0 EndX=-41 EndY=-4 EndZ=0
    g1: LineSegment StartX=-41 StartY=-4 StartZ=0 EndX=-10.875 EndY=-4 EndZ=0
    g2: LineSegment StartX=-10.875 StartY=-4 StartZ=0 EndX=-10.875 EndY=-3.4 EndZ=0
    g3: LineSegment StartX=-10.875 StartY=-3.4 StartZ=0 EndX=-41 EndY=-3.4 EndZ=0
    g4: LineSegment StartX=10.875 StartY=-3.4 StartZ=0 EndX=10.875 EndY=-4 EndZ=0
    g5: LineSegment StartX=10.875 StartY=-4 StartZ=0 EndX=41 EndY=-4 EndZ=0
    g6: LineSegment StartX=41 StartY=-4 StartZ=0 EndX=41 EndY=-3.4 EndZ=0
    g7: LineSegment StartX=41 StartY=-3.4 StartZ=0 EndX=10.875 EndY=-3.4 EndZ=0
  constraints (24):
    c: Coincident(g0,g1)
    c: Coincident(g1,g2)
    c: Coincident(g2,g3)
    c: Coincident(g3,g0)
    c: Vertical(g0)
    c: Vertical(g2)
    c: Horizontal(g1)
    c: Horizontal(g3)
    c: Coincident(g4,g5)
    c: Coincident(g5,g6)
    c: Coincident(g6,g7)
    c: Coincident(g7,g4)
    c: Vertical(g4)
    c: Vertical(g6)
    c: Horizontal(g5)
    c: Horizontal(g7)
    c: Equal(g4,g2)
    c: DistanceY(g0,g0) = 0.6
    c: Distance(g-4,g1) = 1
    c: Horizontal(g4,g2)
    c: Vertical(g-3,g5)
    c: Vertical(g4,g-3)
    c: Vertical(g1,g-4)
    c: Vertical(g0,g-4)
FEATURE [PartDesign::Groove] Groove004
  Angle = 360
  Angle2 = 60
  Axis = (1,0,0)
  Base = (10.875,4,37.25)
  BaseFeature = -> Chamfer
  Placement = pos=(0,0,0) rot=(1,0,0;1.5708rad)
  Profile = -> Sketch017
  ReferenceAxis = -> Sketch017 [Edge6]
  Refine = true
  Suppressed = false
  Type = 0
FEATURE [Sketcher::SketchObject] Sketch018
  ArcFitTolerance = 1e-06
  AttachmentSupport = -> [Groove004]
  ExternalGeometry = -> [Groove004]
  ExternalTypes = [0]
  FullyConstrained = true
  MakeInternals = false
  MapMode = 5
  Placement = pos=(0,0,-37.25) rot=(0,0,1;3.14159rad)
  _ExternalGeoVersion = 0
  sketch-geometry (4):
    g0: LineSegment StartX=-41 StartY=-3.4 StartZ=0 EndX=-41 EndY=-4 EndZ=0
    g1: LineSegment StartX=-41 StartY=-4 StartZ=0 EndX=41 EndY=-4 EndZ=0
    g2: LineSegment StartX=41 StartY=-4 StartZ=0 EndX=41 EndY=-3.4 EndZ=0
    g3: LineSegment StartX=41 StartY=-3.4 StartZ=0 EndX=-41 EndY=-3.4 EndZ=0
  constraints (12):
    c: Coincident(g0,g1)
    c: Coincident(g1,g2)
    c: Coincident(g2,g3)
    c: Coincident(g3,g0)
    c: Vertical(g0)
    c: Vertical(g2)
    c: Horizontal(g1)
    c: Horizontal(g3)
    c: DistanceY(g2,g2) = 0.6
    c: Distance(g-3,g1) = 1
    c: Vertical(g0,g-3)
    c: Vertical(g-3,g1)
FEATURE [PartDesign::Groove] Groove005
  Angle = 360
  Angle2 = 60
  Axis = (-1,0,0)
  Base = (41,4,-37.25)
  BaseFeature = -> Groove004
  Placement = pos=(0,0,0) rot=(1,0,0;1.5708rad)
  Profile = -> Sketch018
  ReferenceAxis = -> Sketch018 [Edge2]
  Refine = true
  Suppressed = false
  Type = 0
FEATURE [Sketcher::SketchObject] Sketch020
  ArcFitTolerance = 1e-06
  AttachmentSupport = -> [Groove005]
  ExternalGeometry = -> [Groove005]
  ExternalTypes = [0]
  FullyConstrained = true
  MakeInternals = false
  MapMode = 5
  Placement = pos=(44,0,0) rot=(0.707107,0,-0.707107;3.14159rad)
  _ExternalGeoVersion = 0
  sketch-geometry (4):
    g0: LineSegment StartX=34.25 StartY=-4 StartZ=0 EndX=34.25 EndY=-3.4 EndZ=0
    g1: LineSegment StartX=34.25 StartY=-3.4 StartZ=0 EndX=-34.25 EndY=-3.4 EndZ=0
    g2: LineSegment StartX=-34.25 StartY=-3.4 StartZ=0 EndX=-34.25 EndY=-4 EndZ=0
    g3: LineSegment StartX=-34.25 StartY=-4 StartZ=0 EndX=34.25 EndY=-4 EndZ=0
  constraints (12):
    c: Coincident(g0,g1)
    c: Coincident(g1,g2)
    c: Coincident(g2,g3)
    c: Coincident(g3,g0)
    c: Vertical(g0)
    c: Vertical(g2)
    c: Horizontal(g1)
    c: Horizontal(g3)
    c: Distance(g3,g-3) = 1
    c: DistanceY(g2,g2) = 0.6
    c: Vertical(g2,g-3)
    c: Vertical(g0,g-3)
FEATURE [PartDesign::Groove] Groove006
  Angle = 360
  Angle2 = 60
  Axis = (2e-16,0,-1)
  Base = (44,4,34.25)
  BaseFeature = -> Groove005
  Placement = pos=(0,0,0) rot=(1,0,0;1.5708rad)
  Profile = -> Sketch020
  ReferenceAxis = -> Sketch020 [Edge4]
  Refine = true
  Reversed = true
  Suppressed = false
  Type = 0
FEATURE [PartDesign::Mirrored] Mirrored
  BaseFeature = -> Groove006
  MirrorPlane = -> YZ_Plane004
  Originals = -> [Groove006]
  Placement = pos=(0,0,0) rot=(1,0,0;1.5708rad)
  Refine = true
  Suppressed = false
  TransformMode = 0
FEATURE [Sketcher::SketchObject] Sketch024
  ArcFitTolerance = 1e-06
  AttachmentSupport = -> [XZ_Plane005]
  ExternalTypes = [0]
  FullyConstrained = true
  MakeInternals = false
  MapMode = 5
  Placement = pos=(0,0,0) rot=(1,0,0;1.5708rad)
  _ExternalGeoVersion = 0
  sketch-geometry (9):
    g0: Circle CenterX=0 CenterY=0 CenterZ=0 NormalX=0 NormalY=0 NormalZ=1 AngleXU=0 Radius=1.4
    g1: LineSegment StartX=-1.6 StartY=2.1 StartZ=0 EndX=-1.6 EndY=-2.1 EndZ=0
    g2: LineSegment StartX=-1.6 StartY=-2.1 StartZ=0 EndX=1.6 EndY=-2.1 EndZ=0
    g3: LineSegment StartX=1.6 StartY=-2.1 StartZ=0 EndX=1.6 EndY=2.1 EndZ=0
    g4: LineSegment StartX=1.6 StartY=2.1 StartZ=0 EndX=-1.6 EndY=2.1 EndZ=0
    g5: LineSegment StartX=-2.5 StartY=3 StartZ=0 EndX=-2.5 EndY=-3 EndZ=0
    g6: LineSegment StartX=-2.5 StartY=-3 StartZ=0 EndX=2.5 EndY=-3 EndZ=0
    g7: LineSegment StartX=2.5 StartY=-3 StartZ=0 EndX=2.5 EndY=3 EndZ=0
    g8: LineSegment StartX=2.5 StartY=3 StartZ=0 EndX=-2.5 EndY=3 EndZ=0
  constraints (24):
    c: Diameter(g0) = 2.8
    c: Coincident(g0,g-1)
    c: Coincident(g1,g2)
    c: Coincident(g2,g3)
    c: Coincident(g3,g4)
    c: Coincident(g4,g1)
    c: Vertical(g1)
    c: Vertical(g3)
    c: Horizontal(g2)
    c: Horizontal(g4)
    c: Coincident(g5,g6)
    c: Coincident(g6,g7)
    c: Coincident(g7,g8)
    c: Coincident(g8,g5)
    c: Vertical(g5)
    c: Vertical(g7)
    c: Horizontal(g6)
    c: Horizontal(g8)
    c: DistanceY(g3,g3) = 4.2
    c: DistanceX(g2,g2) = 3.2
    c: Symmetric(g2,g1,g0)
    c: Symmetric(g6,g5,g0)
    c: DistanceX(g6,g6) = 5
    c: DistanceY(g7,g7) = 6
FEATURE [PartDesign::Pad] Pad012
  Direction = (0,-1,2e-16)
  Length = 3
  Length2 = 10
  Placement = pos=(0,0,0) rot=(1,0,0;1.5708rad)
  Profile = -> Sketch024 [Edge9,Edge7,Edge8,Edge6]
  ReferenceAxis = -> Sketch024 [N_Axis]
  Refine = true
  Reversed = true
  SideType = 0
  Suppressed = false
  Type = 0
  Type2 = 0
FEATURE [PartDesign::Pad] Pad013  label="tmp_fix"
  BaseFeature = -> Pad012
  Direction = (0,-1,2e-16)
  Length = -1
  Length2 = 8
  Placement = pos=(0,0,0) rot=(1,0,0;1.5708rad)
  Profile = -> Sketch024 [Edge1]
  ReferenceAxis = -> Sketch024 [N_Axis]
  Refine = true
  SideType = 1
  Suppressed = false
  Type = 0
  Type2 = 0
FEATURE [PartDesign::Body] Body005  label="buttom(old)"
  AllowCompound = false
  Group = -> [Sketch024,Pad012,Pad013]
  Origin = -> Origin005
  Placement = pos=(41,0,0) rot=(0,0,1;0rad)
  Tip = -> Pad013
FEATURE [Sketcher::SketchObject] Sketch025
  ArcFitTolerance = 1e-06
  AttachmentSupport = -> [Groove003]
  ExternalGeometry = -> [Groove003]
  ExternalTypes = [0]
  FullyConstrained = true
  MakeInternals = false
  MapMode = 5
  Placement = pos=(0,-2,0) rot=(1,0,0;1.5708rad)
  _ExternalGeoVersion = 0
  sketch-geometry (12):
    g0: LineSegment [constr] StartX=-46.25 StartY=38.5 StartZ=0 EndX=-46.25 EndY=-38.5 EndZ=0
    g1: LineSegment [constr] StartX=-46.25 StartY=-38.5 StartZ=0 EndX=46.25 EndY=-38.5 EndZ=0
    g2: LineSegment [constr] StartX=46.25 StartY=-38.5 StartZ=0 EndX=46.25 EndY=38.5 EndZ=0
    g3: LineSegment [constr] StartX=46.25 StartY=38.5 StartZ=0 EndX=-46.25 EndY=38.5 EndZ=0
    g4: LineSegment StartX=-45.25 StartY=38.5 StartZ=0 EndX=45.25 EndY=38.5 EndZ=0
    g5: LineSegment StartX=45.25 StartY=38.5 StartZ=0 EndX=45.25 EndY=-38.5 EndZ=0
    g6: LineSegment StartX=45.25 StartY=-38.5 StartZ=0 EndX=8.5 EndY=-38.5 EndZ=0
    g7: LineSegment StartX=8.5 StartY=-38.5 StartZ=0 EndX=8.5 EndY=-22.5 EndZ=0
    g8: LineSegment StartX=8.5 StartY=-22.5 StartZ=0 EndX=-8.5 EndY=-22.5 EndZ=0
    g9: LineSegment StartX=-8.5 StartY=-22.5 StartZ=0 EndX=-8.5 EndY=-38.5 EndZ=0
    g10: LineSegment StartX=-8.5 StartY=-38.5 StartZ=0 EndX=-45.25 EndY=-38.5 EndZ=0
    g11: LineSegment StartX=-45.25 StartY=38.5 StartZ=0 EndX=-45.25 EndY=-38.5 EndZ=0
  constraints (34):
    c: Coincident(g0,g1)
    c: Coincident(g1,g2)
    c: Coincident(g2,g3)
    c: Coincident(g3,g0)
    c: Vertical(g0)
    c: Vertical(g2)
    c: Horizontal(g1)
    c: Horizontal(g3)
    c: Symmetric(g1,g0,g-1)
    c: DistanceY(g0,g0) = 77
    c: DistanceX(g3,g3) = 92.5
    c: Horizontal(g4)
    c: Coincident(g5,g4)
    c: Vertical(g5)
    c: Coincident(g6,g5)
    c: Horizontal(g6)
    c: Coincident(g7,g6)
    c: Vertical(g7)
    c: Coincident(g8,g7)
    c: Coincident(g9,g8)
    c: Vertical(g9)
    c: Coincident(g10,g9)
    c: Horizontal(g10)
    c: Coincident(g11,g4)
    c: Coincident(g11,g10)
    c: Vertical(g11)
    c: Symmetric(g8,g7,g-2)
    c: Equal(g9,g7)
    c: Horizontal(g8,g-4)
    c: Distance(g2,g5) = 1
    c: Distance(g0,g11) = 1
    c: DistanceX(g8,g8) = 17
    c: PointOnObject(g9,g1)
    c: PointOnObject(g4,g3)
FEATURE [PartDesign::Pocket] Pocket
  BaseFeature = -> Groove003
  Direction = (0,1,-2e-16)
  Length = 0.9
  Length2 = 5
  Placement = pos=(0,0,0) rot=(1,0,0;1.5708rad)
  Profile = -> Sketch025
  ReferenceAxis = -> Sketch025 [N_Axis]
  SideType = 0
  Suppressed = false
  Type = 0
  Type2 = 0
FEATURE [Sketcher::SketchObject] Sketch026
  ArcFitTolerance = 1e-06
  AttachmentSupport = -> [Pocket]
  ExternalTypes = [0]
  FullyConstrained = true
  MakeInternals = false
  MapMode = 5
  Placement = pos=(0,-1.1,0) rot=(1,0,0;1.5708rad)
  _ExternalGeoVersion = 0
  sketch-geometry (8):
    g0: Circle CenterX=41 CenterY=34.25 CenterZ=0 NormalX=0 NormalY=0 NormalZ=1 AngleXU=0 Radius=2.25
    g1: Circle CenterX=41 CenterY=-34.25 CenterZ=0 NormalX=0 NormalY=0 NormalZ=1 AngleXU=0 Radius=2.25
    g2: Circle CenterX=-41 CenterY=-34.25 CenterZ=0 NormalX=0 NormalY=0 NormalZ=1 AngleXU=0 Radius=2.25
    g3: Circle CenterX=-41 CenterY=34.25 CenterZ=0 NormalX=0 NormalY=0 NormalZ=1 AngleXU=0 Radius=2.25
    g4: Circle CenterX=41 CenterY=34.25 CenterZ=0 NormalX=0 NormalY=0 NormalZ=1 AngleXU=0 Radius=1
    g5: Circle CenterX=41 CenterY=-34.25 CenterZ=0 NormalX=0 NormalY=0 NormalZ=1 AngleXU=0 Radius=1
    g6: Circle CenterX=-41 CenterY=-34.25 CenterZ=0 NormalX=0 NormalY=0 NormalZ=1 AngleXU=0 Radius=1
    g7: Circle CenterX=-41 CenterY=34.25 CenterZ=0 NormalX=0 NormalY=0 NormalZ=1 AngleXU=0 Radius=1
  constraints (16):
    c: Diameter(g0) = 4.5
    c: Coincident(g0,g-6)
    c: Coincident(g1,g-3)
    c: Coincident(g2,g-4)
    c: Coincident(g3,g-5)
    c: Equal(g3,g0)
    c: Equal(g2,g0)
    c: Equal(g1,g0)
    c: Coincident(g4,g0)
    c: Equal(g-6,g4)
    c: Coincident(g5,g1)
    c: Coincident(g6,g2)
    c: Coincident(g7,g3)
    c: Equal(g7,g-5)
    c: Equal(g6,g-4)
    c: Equal(g-3,g5)
FEATURE [PartDesign::Pad] Pad014
  BaseFeature = -> Pocket
  Direction = (0,-1,2e-16)
  Length = 0.7
  Length2 = 10
  Placement = pos=(0,0,0) rot=(1,0,0;1.5708rad)
  Profile = -> Sketch026
  ReferenceAxis = -> Sketch026 [N_Axis]
  SideType = 0
  Suppressed = false
  Type = 0
  Type2 = 0
FEATURE [Sketcher::SketchObject] Sketch027
  ArcFitTolerance = 1e-06
  AttachmentSupport = -> [Pad014]
  ExternalTypes = [0]
  FullyConstrained = true
  MakeInternals = false
  MapMode = 5
  Placement = pos=(0,-1.1,0) rot=(1,0,0;1.5708rad)
  _ExternalGeoVersion = 0
  sketch-geometry (4):
    g0: LineSegment StartX=-43.25 StartY=-8 StartZ=0 EndX=-45.25 EndY=-8 EndZ=0
    g1: LineSegment StartX=-45.25 StartY=-8 StartZ=0 EndX=-45.25 EndY=-12 EndZ=0
    g2: LineSegment StartX=-45.25 StartY=-12 StartZ=0 EndX=-43.25 EndY=-12 EndZ=0
    g3: LineSegment StartX=-43.25 StartY=-12 StartZ=0 EndX=-43.25 EndY=-8 EndZ=0
  constraints (12):
    c: Coincident(g0,g1)
    c: Coincident(g1,g2)
    c: Coincident(g2,g3)
    c: Coincident(g3,g0)
    c: Horizontal(g0)
    c: Horizontal(g2)
    c: Vertical(g1)
    c: Vertical(g3)
    c: Distance(g0,g2) = 4
    c: Distance(g-1,g0) = 8
    c: PointOnObject(g1,g-5)
    c: PointOnObject(g2,g-4)
FEATURE [PartDesign::Pocket] Pocket001
  BaseFeature = -> Pad014
  Direction = (0,1,-2e-16)
  Length = 0.5
  Length2 = 5
  Placement = pos=(0,0,0) rot=(1,0,0;1.5708rad)
  Profile = -> Sketch027
  ReferenceAxis = -> Sketch027 [N_Axis]
  SideType = 0
  Suppressed = false
  Type = 0
  Type2 = 0
FEATURE [PartDesign::Body] Body001  label="Clear_plastic_bumper"
  AllowCompound = false
  Group = -> [Sketch015,Pad008,Sketch016,Groove,Groove001,Groove002,Groove003,Sketch025,Pocket,Sketch026,Pad014,Sketch027,Pocket001]
  Origin = -> Origin001
  Placement = pos=(0,2.5,0) rot=(0,0,1;0rad)
  Tip = -> Pocket001
FEATURE [Sketcher::SketchObject] Sketch009
  ArcFitTolerance = 1e-06
  AttachmentSupport = -> [Revolution001]
  ExternalGeometry = -> [Sketch007]
  ExternalTypes = [0]
  FullyConstrained = true
  MakeInternals = false
  MapMode = 5
  Placement = pos=(0,0,-39.5) rot=(0,0,1;3.14159rad)
  _ExternalGeoVersion = 0
  sketch-geometry (8):
    g0: LineSegment StartX=12.5 StartY=-3.2 StartZ=0 EndX=40 EndY=-3.2 EndZ=0
    g1: LineSegment StartX=40 StartY=-3.2 StartZ=0 EndX=40 EndY=-2.7 EndZ=0
    g2: LineSegment StartX=40 StartY=-2.7 StartZ=0 EndX=12.5 EndY=-2.7 EndZ=0
    g3: LineSegment StartX=12.5 StartY=-2.7 StartZ=0 EndX=12.5 EndY=-3.2 EndZ=0
    g4: LineSegment StartX=-40 StartY=-3.2 StartZ=0 EndX=-12.5 EndY=-3.2 EndZ=0
    g5: LineSegment StartX=-12.5 StartY=-3.2 StartZ=0 EndX=-12.5 EndY=-2.7 EndZ=0
    g6: LineSegment StartX=-12.5 StartY=-2.7 StartZ=0 EndX=-40 EndY=-2.7 EndZ=0
    g7: LineSegment StartX=-40 StartY=-2.7 StartZ=0 EndX=-40 EndY=-3.2 EndZ=0
  constraints (23):
    c: Coincident(g0,g1)
    c: Coincident(g1,g2)
    c: Coincident(g2,g3)
    c: Coincident(g3,g0)
    c: Horizontal(g0)
    c: Horizontal(g2)
    c: Vertical(g1)
    c: Vertical(g3)
    c: Equal(g3,g-3)
    c: Horizontal(g-3,g2)
    c: Coincident(g4,g5)
    c: Coincident(g5,g6)
    c: Coincident(g6,g7)
    c: Coincident(g7,g4)
    c: Horizontal(g4)
    c: Horizontal(g6)
    c: Vertical(g5)
    c: Vertical(g7)
    c: Symmetric(g2,g5,g-2)
    c: Distance(g3,g5) = 25
    c: Distance(g1,g7) = 80
    c: Equal(g6,g2)
    c: Equal(g5,g-3)
FEATURE [PartDesign::Revolution] Revolution002
  Angle = 360
  Angle2 = 60
  Axis = (-1,0,0)
  Base = (46.25,3.2,-39.5)
  BaseFeature = -> Revolution001
  FuseOrder = 1
  Placement = pos=(0,0,0) rot=(1,0,0;1.5708rad)
  Profile = -> Sketch009
  ReferenceAxis = -> Revolution001 [Edge24]
  Refine = true
  Suppressed = false
  Type = 0
FEATURE [Sketcher::SketchObject] Sketch010
  ArcFitTolerance = 1e-06
  AttachmentSupport = -> [Revolution002]
  ExternalGeometry = -> [Sketch007]
  ExternalTypes = [0]
  FullyConstrained = true
  MakeInternals = false
  MapMode = 5
  Placement = pos=(-46.25,0,0) rot=(0.707107,0,0.707107;3.14159rad)
  _ExternalGeoVersion = 0
  sketch-geometry (4):
    g0: LineSegment StartX=10 StartY=-3.2 StartZ=0 EndX=10 EndY=-2.7 EndZ=0
    g1: LineSegment StartX=10 StartY=-2.7 StartZ=0 EndX=-30 EndY=-2.7 EndZ=0
    g2: LineSegment StartX=-30 StartY=-2.7 StartZ=0 EndX=-30 EndY=-3.2 EndZ=0
    g3: LineSegment StartX=-30 StartY=-3.2 StartZ=0 EndX=10 EndY=-3.2 EndZ=0
  constraints (12):
    c: Coincident(g0,g1)
    c: Coincident(g1,g2)
    c: Coincident(g2,g3)
    c: Coincident(g3,g0)
    c: Vertical(g0)
    c: Vertical(g2)
    c: Horizontal(g1)
    c: Horizontal(g3)
    c: Equal(g2,g-3)
    c: Horizontal(g-3,g0)
    c: DistanceX(g1,g1) = 40
    c: Distance(g-2,g0) = 10
FEATURE [PartDesign::Mirrored] Mirrored002
  BaseFeature = -> Revolution002
  MirrorPlane = -> YZ_Plane003
  Originals = -> [Revolution001]
  Placement = pos=(0,0,0) rot=(1,0,0;1.5708rad)
  Suppressed = false
  TransformMode = 0
FEATURE [PartDesign::Body] Body003  label="Front"
  AllowCompound = false
  Group = -> [Sketch004,Pad004,Sketch005,Pad005,Sketch006,Pad006,Sketch007,Revolution,Sketch008,Revolution001,Sketch009,Revolution002,Sketch010,Mirrored002]
  Origin = -> Origin003
  Placement = pos=(0,-2.8,0) rot=(0,0,1;0rad)
  Tip = -> Mirrored002
FEATURE [Sketcher::SketchObject] Sketch028
  ArcFitTolerance = 1e-06
  AttachmentSupport = -> [XZ_Plane006]
  ExternalTypes = [0]
  FullyConstrained = true
  MakeInternals = false
  MapMode = 5
  Placement = pos=(0,0,0) rot=(1,0,0;1.5708rad)
  _ExternalGeoVersion = 0
  sketch-geometry (25):
    g0: LineSegment StartX=-4.75 StartY=0.25 StartZ=0 EndX=-4.75 EndY=-0.25 EndZ=0
    g1: LineSegment StartX=-3.25 StartY=-1.75 StartZ=0 EndX=3.25 EndY=-1.75 EndZ=0
    g2: LineSegment StartX=4.75 StartY=-0.25 StartZ=0 EndX=4.75 EndY=0.25 EndZ=0
    g3: LineSegment StartX=3.25 StartY=1.75 StartZ=0 EndX=-3.25 EndY=1.75 EndZ=0
    g4: ArcOfCircle CenterX=-3.25 CenterY=0.25 CenterZ=0 NormalX=0 NormalY=0 NormalZ=1 AngleXU=0 Radius=1.5 StartAngle=1.5708 EndAngle=3.14159
    g5: ArcOfCircle CenterX=-3.25 CenterY=-0.25 CenterZ=0 NormalX=0 NormalY=0 NormalZ=1 AngleXU=0 Radius=1.5 StartAngle=3.14159 EndAngle=4.71239
    g6: ArcOfCircle CenterX=3.25 CenterY=-0.25 CenterZ=0 NormalX=0 NormalY=0 NormalZ=1 AngleXU=0 Radius=1.5 StartAngle=4.71239 EndAngle=6.28319
    g7: ArcOfCircle CenterX=3.25 CenterY=0.25 CenterZ=0 NormalX=0 NormalY=0 NormalZ=1 AngleXU=0 Radius=1.5 StartAngle=0 EndAngle=1.5708
    g8: GeomPoint [constr] X=-4.75 Y=1.75 Z=0
    g9: GeomPoint [constr] X=4.75 Y=-1.75 Z=0
    g10: LineSegment StartX=-5.55 StartY=0.25 StartZ=0 EndX=-5.55 EndY=-0.25 EndZ=0
    g11: LineSegment StartX=-3.25 StartY=-2.55 StartZ=0 EndX=3.25 EndY=-2.55 EndZ=0
    g12: LineSegment StartX=5.55 StartY=-0.25 StartZ=0 EndX=5.55 EndY=0.25 EndZ=0
    g13: LineSegment StartX=3.25 StartY=2.55 StartZ=0 EndX=-3.25 EndY=2.55 EndZ=0
    g14: ArcOfCircle CenterX=-3.25 CenterY=0.25 CenterZ=0 NormalX=0 NormalY=0 NormalZ=1 AngleXU=0 Radius=2.3 StartAngle=1.5708 EndAngle=3.14159
    g15: ArcOfCircle CenterX=-3.25 CenterY=-0.25 CenterZ=0 NormalX=0 NormalY=0 NormalZ=1 AngleXU=0 Radius=2.3 StartAngle=3.14159 EndAngle=4.71239
    g16: ArcOfCircle CenterX=3.25 CenterY=-0.25 CenterZ=0 NormalX=0 NormalY=0 NormalZ=1 AngleXU=0 Radius=2.3 StartAngle=4.71239 EndAngle=6.28319
    g17: ArcOfCircle CenterX=3.25 CenterY=0.25 CenterZ=0 NormalX=0 NormalY=0 NormalZ=1 AngleXU=0 Radius=2.3 StartAngle=0 EndAngle=1.5708
    g18: GeomPoint [constr] X=-5.55 Y=2.55 Z=0
    g19: GeomPoint [constr] X=5.55 Y=-2.55 Z=0
    g20: LineSegment StartX=-3.25 StartY=-2.55 StartZ=0 EndX=-8.25 EndY=-2.55 EndZ=0
    g21: LineSegment StartX=-5.55 StartY=-0.25 StartZ=0 EndX=-5.55 EndY=-0.3 EndZ=0
    g22: LineSegment StartX=-8.25 StartY=-0.55 StartZ=0 EndX=-5.8 EndY=-0.55 EndZ=0
    g23: ArcOfCircle CenterX=-5.8 CenterY=-0.3 CenterZ=0 NormalX=0 NormalY=0 NormalZ=1 AngleXU=0 Radius=0.25 StartAngle=4.71239 EndAngle=6.28319
    g24: ArcOfCircle CenterX=-8.25 CenterY=-1.55 CenterZ=0 NormalX=0 NormalY=0 NormalZ=1 AngleXU=0 Radius=1 StartAngle=1.5708 EndAngle=4.71239
  constraints (61):
    c: Tangent(g0,g4) = -1.5708
    c: Tangent(g0,g5) = -1.5708
    c: Tangent(g1,g5) = -1.5708
    c: Tangent(g1,g6) = -1.5708
    c: Tangent(g2,g6) = -1.5708
    c: Tangent(g2,g7) = -1.5708
    c: Tangent(g3,g7) = -1.5708
    c: Tangent(g3,g4) = -1.5708
    c: Vertical(g0)
    c: Vertical(g2)
    c: Horizontal(g1)
    c: Equal(g4,g5)
    c: Equal(g5,g6)
    c: Equal(g6,g7)
    c: PointOnObject(g8,g0)
    c: PointOnObject(g8,g3)
    c: PointOnObject(g9,g1)
    c: PointOnObject(g9,g2)
    c: Radius(g5) = 1.5
    c: Distance(g2,g0) = 9.5
    c: Distance(g1,g3) = 3.5
    c: Horizontal(g3)
    c: Symmetric(g7,g5,g-1)
    c: Tangent(g10,g14) = -1.5708
    c: Tangent(g10,g15) = -1.5708
    c: Tangent(g11,g15) = -1.5708
    c: Tangent(g11,g16) = -1.5708
    c: Tangent(g12,g16) = -1.5708
    c: Tangent(g12,g17) = -1.5708
    c: Tangent(g13,g17) = -1.5708
    c: Tangent(g13,g14) = -1.5708
    c: Vertical(g10)
    c: Vertical(g12)
    c: Horizontal(g11)
    c: Horizontal(g13)
    c: Equal(g14,g15)
    c: Equal(g15,g16)
    c: Equal(g16,g17)
    c: PointOnObject(g18,g10)
    c: PointOnObject(g18,g13)
    c: PointOnObject(g19,g11)
    c: PointOnObject(g19,g12)
    c: Coincident(g16,g6)
    c: Coincident(g14,g4)
    c: Coincident(g20,g11)
    c: Horizontal(g20)
    c: Coincident(g21,g10)
    c: Vertical(g21)
    c: Horizontal(g22)
    c: Coincident(g23,g21)
    c: Coincident(g23,g22)
    c: Horizontal(g23,g21)
    c: Vertical(g23,g22)
    c: Coincident(g24,g22)
    c: Coincident(g24,g20)
    c: Vertical(g24,g20)
    c: Vertical(g20,g22)
    c: Radius(g15) = 2.3
    c: Radius(g23) = 0.25
    c: DistanceX(g20,g20) = 5
    c: Radius(g24) = 1
FEATURE [PartDesign::Pad] Pad015
  Direction = (0,-1,2e-16)
  Length = 1.5
  Length2 = 10
  Placement = pos=(0,0,0) rot=(1,0,0;1.5708rad)
  Profile = -> Sketch028 [Edge13,Edge12,Edge11,Edge10,Edge14,Edge9,Edge21,Edge16,Edge17,Edge19,Edge18,Edge20,Edge7,Edge8,Edge1,Edge2,Edge3,Edge4,Edge5,Edge6]
  ReferenceAxis = -> Sketch028 [N_Axis]
  SideType = 0
  Suppressed = false
  Type = 0
  Type2 = 0
FEATURE [PartDesign::Pad] Pad016
  BaseFeature = -> Pad015
  Direction = (0,-1,2e-16)
  Length = 7
  Length2 = 10
  Placement = pos=(0,0,0) rot=(1,0,0;1.5708rad)
  Profile = -> Sketch028 [Edge15,Edge16,Edge17,Edge18,Edge19,Edge20,Edge21,Edge9,Edge8,Edge1,Edge2,Edge3,Edge4,Edge5,Edge6,Edge7]
  ReferenceAxis = -> Sketch028 [N_Axis]
  SideType = 0
  Suppressed = false
  Type = 0
  Type2 = 0
FEATURE [PartDesign::Body] Body006  label="clear_plastic_usb"
  AllowCompound = false
  Group = -> [Sketch028,Pad015,Pad016]
  Origin = -> Origin006
  Placement = pos=(0,0,35.7) rot=(0,0,1;0rad)
  Tip = -> Pad016
FEATURE [Sketcher::SketchObject] Sketch029
  ArcFitTolerance = 1e-06
  AttachmentSupport = -> [Pad009]
  ExternalGeometry = -> [Pad009]
  ExternalTypes = [0]
  FullyConstrained = true
  MakeInternals = false
  MapMode = 5
  Placement = pos=(0,5,0) rot=(-1,0,0;1.5708rad)
  _ExternalGeoVersion = 0
  sketch-geometry (10):
    g0: LineSegment StartX=-5.75 StartY=-35.5 StartZ=0 EndX=-5.75 EndY=-36 EndZ=0
    g1: LineSegment StartX=-3.25 StartY=-38.5 StartZ=0 EndX=3.25 EndY=-38.5 EndZ=0
    g2: LineSegment StartX=5.75 StartY=-36 StartZ=0 EndX=5.75 EndY=-35.5 EndZ=0
    g3: LineSegment StartX=3.25 StartY=-33 StartZ=0 EndX=-3.25 EndY=-33 EndZ=0
    g4: ArcOfCircle CenterX=-3.25 CenterY=-35.5 CenterZ=0 NormalX=0 NormalY=0 NormalZ=1 AngleXU=0 Radius=2.5 StartAngle=1.5708 EndAngle=3.14159
    g5: ArcOfCircle CenterX=-3.25 CenterY=-36 CenterZ=0 NormalX=0 NormalY=0 NormalZ=1 AngleXU=0 Radius=2.5 StartAngle=3.14159 EndAngle=4.71239
    g6: ArcOfCircle CenterX=3.25 CenterY=-36 CenterZ=0 NormalX=0 NormalY=0 NormalZ=1 AngleXU=0 Radius=2.5 StartAngle=4.71239 EndAngle=6.28319
    g7: ArcOfCircle CenterX=3.25 CenterY=-35.5 CenterZ=0 NormalX=0 NormalY=0 NormalZ=1 AngleXU=0 Radius=2.5 StartAngle=3e-16 EndAngle=1.5708
    g8: GeomPoint [constr] X=-5.75 Y=-33 Z=0
    g9: GeomPoint [constr] X=5.75 Y=-38.5 Z=0
  constraints (22):
    c: Tangent(g0,g4) = -1.5708
    c: Tangent(g0,g5) = -1.5708
    c: Tangent(g1,g5) = -1.5708
    c: Tangent(g1,g6) = -1.5708
    c: Tangent(g2,g6) = -1.5708
    c: Tangent(g2,g7) = -1.5708
    c: Tangent(g3,g7) = -1.5708
    c: Tangent(g3,g4) = -1.5708
    c: Vertical(g0)
    c: Vertical(g2)
    c: Horizontal(g1)
    c: Horizontal(g3)
    c: Equal(g4,g5)
    c: Equal(g5,g6)
    c: Equal(g6,g7)
    c: PointOnObject(g8,g0)
    c: PointOnObject(g8,g3)
    c: PointOnObject(g9,g1)
    c: PointOnObject(g9,g2)
    c: Radius(g5) = 2.5
    c: Coincident(g4,g-3)
    c: Coincident(g6,g-4)
FEATURE [PartDesign::Pocket] Pocket002
  BaseFeature = -> Mirrored
  Direction = (0,-1,-2e-16)
  Length = 5
  Length2 = 5
  Placement = pos=(0,0,0) rot=(1,0,0;1.5708rad)
  Profile = -> Sketch029
  ReferenceAxis = -> Sketch029 [N_Axis]
  SideType = 0
  Suppressed = false
  Type = 1
  Type2 = 0
FEATURE [PartDesign::Body] Body004  label="bumper"
  AllowCompound = false
  Group = -> [Sketch011,Pad009,Pad010,Chamfer,Sketch017,Groove004,Sketch018,Groove005,Sketch020,Groove006,Mirrored,Sketch029,Pocket002]
  Origin = -> Origin004
  Placement = pos=(0,2.5,0) rot=(0,0,1;0rad)
  Tip = -> Pocket002
FEATURE [Sketcher::SketchObject] Sketch030
  ArcFitTolerance = 1e-06
  AttachmentSupport = -> [XZ_Plane007]
  ExternalTypes = [0]
  FullyConstrained = true
  MakeInternals = false
  MapMode = 5
  Placement = pos=(0,0,0) rot=(1,0,0;1.5708rad)
  _ExternalGeoVersion = 0
  sketch-geometry (26):
    g0: Circle [constr] CenterX=0 CenterY=0 CenterZ=0 NormalX=0 NormalY=0 NormalZ=1 AngleXU=0 Radius=1.25
    g1: LineSegment StartX=-1.08253 StartY=-1.25 StartZ=0 EndX=1.08253 EndY=-1.25 EndZ=0
    g2: LineSegment StartX=-0.541266 StartY=1.5625 StartZ=0 EndX=-1.6238 EndY=-0.3125 EndZ=0
    g3: LineSegment StartX=0.541266 StartY=1.5625 StartZ=0 EndX=1.6238 EndY=-0.3125 EndZ=0
    g4: ArcOfCircle CenterX=-1e-16 CenterY=1.25 CenterZ=0 NormalX=0 NormalY=0 NormalZ=1 AngleXU=0 Radius=0.625 StartAngle=0.523599 EndAngle=2.61799
    g5: ArcOfCircle CenterX=1.08253 CenterY=-0.625 CenterZ=0 NormalX=0 NormalY=0 NormalZ=1 AngleXU=0 Radius=0.625 StartAngle=4.71239 EndAngle=6.80678
    g6: ArcOfCircle CenterX=-1.08253 CenterY=-0.625 CenterZ=0 NormalX=0 NormalY=0 NormalZ=1 AngleXU=0 Radius=0.625 StartAngle=2.61799 EndAngle=4.71239
    g7: LineSegment [constr] StartX=-0.541266 StartY=1.5625 StartZ=0 EndX=-1e-16 EndY=1.25 EndZ=0
    g8: LineSegment [constr] StartX=-1e-16 StartY=1.25 StartZ=0 EndX=0.541266 EndY=1.5625 EndZ=0
    g9: LineSegment [constr] StartX=-1.6238 StartY=-0.3125 StartZ=0 EndX=-1.08253 EndY=-0.625 EndZ=0
    g10: LineSegment [constr] StartX=1.08253 StartY=-0.625 StartZ=0 EndX=1.6238 EndY=-0.3125 EndZ=0
    g11: GeomPoint [constr] X=0 Y=-1.25 Z=0
    g12: LineSegment StartX=-2.25 StartY=1.75 StartZ=0 EndX=-2.25 EndY=-1.75 EndZ=0
    g13: LineSegment StartX=-1.25 StartY=-2.75 StartZ=0 EndX=1.25 EndY=-2.75 EndZ=0
    g14: LineSegment StartX=2.25 StartY=-1.75 StartZ=0 EndX=2.25 EndY=1.75 EndZ=0
    g15: LineSegment StartX=1.25 StartY=2.75 StartZ=0 EndX=-1.25 EndY=2.75 EndZ=0
    g16: ArcOfCircle CenterX=-1.25 CenterY=1.75 CenterZ=0 NormalX=0 NormalY=0 NormalZ=1 AngleXU=0 Radius=1 StartAngle=1.5708 EndAngle=3.14159
    g17: ArcOfCircle CenterX=-1.25 CenterY=-1.75 CenterZ=0 NormalX=0 NormalY=0 NormalZ=1 AngleXU=0 Radius=1 StartAngle=3.14159 EndAngle=4.71239
    g18: ArcOfCircle CenterX=1.25 CenterY=-1.75 CenterZ=0 NormalX=0 NormalY=0 NormalZ=1 AngleXU=0 Radius=1 StartAngle=4.71239 EndAngle=6.28319
    g19: ArcOfCircle CenterX=1.25 CenterY=1.75 CenterZ=0 NormalX=0 NormalY=0 NormalZ=1 AngleXU=0 Radius=1 StartAngle=0 EndAngle=1.5708
    g20: GeomPoint [constr] X=-2.25 Y=2.75 Z=0
    g21: GeomPoint [constr] X=2.25 Y=-2.75 Z=0
    g22: LineSegment StartX=-1.75 StartY=2.25 StartZ=0 EndX=-1.75 EndY=-2.25 EndZ=0
    g23: LineSegment StartX=-1.75 StartY=-2.25 StartZ=0 EndX=1.75 EndY=-2.25 EndZ=0
    g24: LineSegment StartX=1.75 StartY=-2.25 StartZ=0 EndX=1.75 EndY=2.25 EndZ=0
    g25: LineSegment StartX=1.75 StartY=2.25 StartZ=0 EndX=-1.75 EndY=2.25 EndZ=0
  constraints (66):
    c: Diameter(g0) = 2.5
    c: Horizontal(g1)
    c: Coincident(g4,g2)
    c: Coincident(g4,g3)
    c: Coincident(g5,g1)
    c: Coincident(g5,g3)
    c: Coincident(g6,g1)
    c: Coincident(g6,g2)
    c: Equal(g4,g6)
    c: Equal(g6,g5)
    c: Vertical(g1,g6)
    c: Vertical(g1,g5)
    c: PointOnObject(g6,g0)
    c: PointOnObject(g5,g0)
    c: Equal(g1,g2)
    c: Equal(g2,g3)
    c: Coincident(g7,g2)
    c: Coincident(g7,g4)
    c: Coincident(g8,g4)
    c: Coincident(g8,g3)
    c: PointOnObject(g4,g0)
    c: Perpendicular(g3,g8)
    c: Perpendicular(g2,g7)
    c: Coincident(g9,g2)
    c: Coincident(g9,g6)
    c: Coincident(g10,g5)
    c: Coincident(g10,g3)
    c: Perpendicular(g3,g10)
    c: Perpendicular(g2,g9)
    c: PointOnObject(g11,g0)
    c: Symmetric(g1,g1,g11)
    c: Coincident(g-1,g0)
    c: Tangent(g12,g16) = -1.5708
    c: Tangent(g12,g17) = -1.5708
    c: Tangent(g13,g17) = -1.5708
    c: Tangent(g13,g18) = -1.5708
    c: Tangent(g14,g18) = -1.5708
    c: Tangent(g14,g19) = -1.5708
    c: Tangent(g15,g19) = -1.5708
    c: Tangent(g15,g16) = -1.5708
    c: Vertical(g12)
    c: Vertical(g14)
    c: Horizontal(g13)
    c: Horizontal(g15)
    c: Equal(g16,g17)
    c: Equal(g17,g18)
    c: Equal(g18,g19)
    c: PointOnObject(g20,g12)
    c: PointOnObject(g20,g15)
    c: PointOnObject(g21,g13)
    c: PointOnObject(g21,g14)
    c: Symmetric(g19,g17,g0)
    c: Distance(g13,g15) = 5.5
    c: Distance(g14,g12) = 4.5
    c: Coincident(g22,g23)
    c: Coincident(g23,g24)
    c: Coincident(g24,g25)
    c: Coincident(g25,g22)
    c: Vertical(g22)
    c: Vertical(g24)
    c: Horizontal(g23)
    c: Horizontal(g25)
    c: Radius(g19) = 1
    c: Symmetric(g23,g22,g0)
    c: DistanceX(g25,g25) = 3.5
    c: DistanceY(g24,g24) = 4.5
FEATURE [PartDesign::Pad] Pad019
  Direction = (0,-1,2e-16)
  Length = 2.8
  Length2 = 10
  Placement = pos=(0,0,0) rot=(1,0,0;1.5708rad)
  Profile = -> Sketch030 [Edge13,Edge12,Edge11,Edge10,Edge9,Edge8,Edge7,Edge14]
  ReferenceAxis = -> Sketch030 [N_Axis]
  SideType = 0
  Suppressed = false
  Type = 0
  Type2 = 0
FEATURE [PartDesign::Pad] Pad020
  BaseFeature = -> Pad019
  Direction = (0,-1,2e-16)
  Length = 6
  Length2 = 10
  Placement = pos=(0,0,0) rot=(1,0,0;1.5708rad)
  Profile = -> Sketch030 [Edge4,Edge5,Edge6,Edge1,Edge2,Edge3]
  ReferenceAxis = -> Sketch030 [N_Axis]
  SideType = 0
  Suppressed = false
  Type = 0
  Type2 = 0
FEATURE [PartDesign::Body] Body007  label="Buttom(UP-DOWN)"
  AllowCompound = false
  Group = -> [Sketch030,Pad019,Pad020]
  Origin = -> Origin007
  Placement = pos=(40.9,0,20.2) rot=(0,0,1;0rad)
  Tip = -> Pad020
FEATURE [Sketcher::SketchObject] Sketch031
  ArcFitTolerance = 1e-06
  AttachmentSupport = -> [XZ_Plane008]
  ExternalTypes = [0]
  FullyConstrained = true
  MakeInternals = false
  MapMode = 5
  Placement = pos=(0,0,0) rot=(1,0,0;1.5708rad)
  _ExternalGeoVersion = 0
  sketch-geometry (24):
    g0: LineSegment StartX=-1.75 StartY=1.25 StartZ=0 EndX=-1.75 EndY=-1.25 EndZ=0
    g1: LineSegment StartX=-1.25 StartY=-1.75 StartZ=0 EndX=1.25 EndY=-1.75 EndZ=0
    g2: LineSegment StartX=1.75 StartY=-1.25 StartZ=0 EndX=1.75 EndY=1.25 EndZ=0
    g3: LineSegment StartX=1.25 StartY=1.75 StartZ=0 EndX=-1.25 EndY=1.75 EndZ=0
    g4: ArcOfCircle CenterX=-1.25 CenterY=1.25 CenterZ=0 NormalX=0 NormalY=0 NormalZ=1 AngleXU=0 Radius=0.5 StartAngle=1.5708 EndAngle=3.14159
    g5: ArcOfCircle CenterX=-1.25 CenterY=-1.25 CenterZ=0 NormalX=0 NormalY=0 NormalZ=1 AngleXU=0 Radius=0.5 StartAngle=3.14159 EndAngle=4.71239
    g6: ArcOfCircle CenterX=1.25 CenterY=-1.25 CenterZ=0 NormalX=0 NormalY=0 NormalZ=1 AngleXU=0 Radius=0.5 StartAngle=4.71239 EndAngle=6.28319
    g7: ArcOfCircle CenterX=1.25 CenterY=1.25 CenterZ=0 NormalX=0 NormalY=0 NormalZ=1 AngleXU=0 Radius=0.5 StartAngle=0 EndAngle=1.5708
    g8: GeomPoint [constr] X=-1.75 Y=1.75 Z=0
    g9: GeomPoint [constr] X=1.75 Y=-1.75 Z=0
    g10: LineSegment StartX=-2.25 StartY=1.75 StartZ=0 EndX=-2.25 EndY=-1.75 EndZ=0
    g11: LineSegment StartX=-1.25 StartY=-2.75 StartZ=0 EndX=1.25 EndY=-2.75 EndZ=0
    g12: LineSegment StartX=2.25 StartY=-1.75 StartZ=0 EndX=2.25 EndY=1.75 EndZ=0
    g13: LineSegment StartX=1.25 StartY=2.75 StartZ=0 EndX=-1.25 EndY=2.75 EndZ=0
    g14: ArcOfCircle CenterX=-1.25 CenterY=1.75 CenterZ=0 NormalX=0 NormalY=0 NormalZ=1 AngleXU=0 Radius=1 StartAngle=1.5708 EndAngle=3.14159
    g15: ArcOfCircle CenterX=-1.25 CenterY=-1.75 CenterZ=0 NormalX=0 NormalY=0 NormalZ=1 AngleXU=0 Radius=1 StartAngle=3.14159 EndAngle=4.71239
    g16: ArcOfCircle CenterX=1.25 CenterY=-1.75 CenterZ=0 NormalX=0 NormalY=0 NormalZ=1 AngleXU=0 Radius=1 StartAngle=4.71239 EndAngle=6.28319
    g17: ArcOfCircle CenterX=1.25 CenterY=1.75 CenterZ=0 NormalX=0 NormalY=0 NormalZ=1 AngleXU=0 Radius=1 StartAngle=1e-16 EndAngle=1.5708
    g18: GeomPoint [constr] X=-2.25 Y=2.75 Z=0
    g19: GeomPoint [constr] X=2.25 Y=-2.75 Z=0
    g20: LineSegment StartX=-1.75 StartY=2.25 StartZ=0 EndX=-1.75 EndY=-2.25 EndZ=0
    g21: LineSegment StartX=-1.75 StartY=-2.25 StartZ=0 EndX=1.75 EndY=-2.25 EndZ=0
    g22: LineSegment StartX=1.75 StartY=-2.25 StartZ=0 EndX=1.75 EndY=2.25 EndZ=0
    g23: LineSegment StartX=1.75 StartY=2.25 StartZ=0 EndX=-1.75 EndY=2.25 EndZ=0
  constraints (57):
    c: Tangent(g0,g4) = -1.5708
    c: Tangent(g0,g5) = -1.5708
    c: Tangent(g1,g5) = -1.5708
    c: Tangent(g1,g6) = -1.5708
    c: Tangent(g2,g6) = -1.5708
    c: Tangent(g2,g7) = -1.5708
    c: Tangent(g3,g7) = -1.5708
    c: Tangent(g3,g4) = -1.5708
    c: Vertical(g0)
    c: Vertical(g2)
    c: Horizontal(g1)
    c: Horizontal(g3)
    c: Equal(g4,g5)
    c: Equal(g5,g6)
    c: Equal(g6,g7)
    c: PointOnObject(g8,g0)
    c: PointOnObject(g8,g3)
    c: PointOnObject(g9,g1)
    c: PointOnObject(g9,g2)
    c: Distance(g0,g2) = 3.5
    c: Equal(g0,g3)
    c: Tangent(g10,g14) = -1.5708
    c: Tangent(g10,g15) = -1.5708
    c: Tangent(g11,g15) = -1.5708
    c: Tangent(g11,g16) = -1.5708
    c: Tangent(g12,g16) = -1.5708
    c: Tangent(g12,g17) = -1.5708
    c: Tangent(g13,g17) = -1.5708
    c: Tangent(g13,g14) = -1.5708
    c: Vertical(g10)
    c: Vertical(g12)
    c: Horizontal(g11)
    c: Horizontal(g13)
    c: Equal(g14,g15)
    c: Equal(g15,g16)
    c: Equal(g16,g17)
    c: PointOnObject(g18,g10)
    c: PointOnObject(g18,g13)
    c: PointOnObject(g19,g11)
    c: PointOnObject(g19,g12)
    c: Distance(g11,g13) = 5.5
    c: Distance(g12,g10) = 4.5
    c: Coincident(g20,g21)
    c: Coincident(g21,g22)
    c: Coincident(g22,g23)
    c: Coincident(g23,g20)
    c: Vertical(g20)
    c: Vertical(g22)
    c: Horizontal(g21)
    c: Horizontal(g23)
    c: Radius(g17) = 1
    c: DistanceX(g23,g23) = 3.5
    c: DistanceY(g22,g22) = 4.5
    c: Radius(g7) = 0.5
    c: Symmetric(g5,g7,g-1)
    c: Symmetric(g20,g22,g-1)
    c: Symmetric(g15,g17,g-1)
FEATURE [PartDesign::Pad] Pad024
  Direction = (0,-1,2e-16)
  Length = 2.8
  Length2 = 10
  Placement = pos=(0,0,0) rot=(1,0,0;1.5708rad)
  Profile = -> Sketch031 [Edge14,Edge13,Edge15,Edge16,Edge9,Edge10,Edge11,Edge12]
  ReferenceAxis = -> Sketch031 [N_Axis]
  SideType = 0
  Suppressed = false
  Type = 0
  Type2 = 0
FEATURE [PartDesign::Pad] Pad025
  BaseFeature = -> Pad024
  Direction = (0,-1,2e-16)
  Length = 6
  Length2 = 10
  Placement = pos=(0,0,0) rot=(1,0,0;1.5708rad)
  Profile = -> Sketch031 [Edge7,Edge6,Edge5,Edge4,Edge3,Edge1,Edge2,Edge8]
  ReferenceAxis = -> Sketch031 [N_Axis]
  SideType = 0
  Suppressed = false
  Type = 0
  Type2 = 0
FEATURE [PartDesign::Body] Body008  label="Buttom(SET)"
  AllowCompound = false
  Group = -> [Sketch031,Pad024,Pad025]
  Origin = -> Origin008
  Placement = pos=(41,0,-19.5) rot=(0,0,1;0rad)
  Tip = -> Pad025
FEATURE [App::Point] Origin010  label="Origin"
  Role = Origin
FEATURE [App::Point] Origin012  label="Origin"
  Role = Origin
FEATURE [App::Point] Origin013  label="Origin"
  Role = Origin
FEATURE [App::Point] Origin014  label="Origin"
  Role = Origin
FEATURE [App::Point] Origin015  label="Origin"
  Role = Origin
FEATURE [App::Point] Origin016  label="Origin"
  Role = Origin
FEATURE [App::Point] Origin017  label="Origin"
  Role = Origin
FEATURE [Mesh::Feature] Bolt__Meshed_  label="Bolt (Meshed)"
  Placement = pos=(0,0,0) rot=(1,0,0;1.5708rad)
FEATURE [App::Point] Origin019
  Role = Origin
FEATURE [Sketcher::SketchObject] Sketch039
  ArcFitTolerance = 1e-06
  AttachmentSupport = -> [XZ_Plane009]
  ExternalTypes = [0]
  FullyConstrained = true
  MakeInternals = false
  MapMode = 5
  Placement = pos=(0,0,0) rot=(1,0,0;1.5708rad)
  _ExternalGeoVersion = 0
  sketch-geometry (102):
    g0: LineSegment StartX=2.875 StartY=4.125 StartZ=0 EndX=-2.875 EndY=4.125 EndZ=0
    g1: LineSegment StartX=-4.125 StartY=2.875 StartZ=0 EndX=-4.125 EndY=-2.875 EndZ=0
    g2: LineSegment StartX=-2.875 StartY=-4.125 StartZ=0 EndX=2.875 EndY=-4.125 EndZ=0
    g3: LineSegment StartX=4.125 StartY=-2.875 StartZ=0 EndX=4.125 EndY=2.875 EndZ=0
    g4: ArcOfCircle CenterX=2.875 CenterY=2.875 CenterZ=0 NormalX=0 NormalY=0 NormalZ=1 AngleXU=0 Radius=1.25 StartAngle=0 EndAngle=1.5708
    g5: ArcOfCircle CenterX=-2.875 CenterY=2.875 CenterZ=0 NormalX=0 NormalY=0 NormalZ=1 AngleXU=0 Radius=1.25 StartAngle=1.5708 EndAngle=3.14159
    g6: ArcOfCircle CenterX=-2.875 CenterY=-2.875 CenterZ=0 NormalX=0 NormalY=0 NormalZ=1 AngleXU=0 Radius=1.25 StartAngle=3.14159 EndAngle=4.71239
    g7: ArcOfCircle CenterX=2.875 CenterY=-2.875 CenterZ=0 NormalX=0 NormalY=0 NormalZ=1 AngleXU=0 Radius=1.25 StartAngle=4.71239 EndAngle=6.28319
    g8: GeomPoint [constr] X=4.125 Y=4.125 Z=0
    g9: GeomPoint [constr] X=-4.125 Y=-4.125 Z=0
    g10: Circle [constr] CenterX=40.75 CenterY=0 CenterZ=0 NormalX=0 NormalY=0 NormalZ=1 AngleXU=0 Radius=1.5
    g11: Circle [constr] CenterX=40.75 CenterY=-19.6 CenterZ=0 NormalX=0 NormalY=0 NormalZ=1 AngleXU=0 Radius=1.5
    g12: Circle [constr] CenterX=40.75 CenterY=19.6 CenterZ=0 NormalX=0 NormalY=0 NormalZ=1 AngleXU=0 Radius=1.5
    g13: Circle CenterX=-19 CenterY=0 CenterZ=0 NormalX=0 NormalY=0 NormalZ=1 AngleXU=0 Radius=1.5
    g14: LineSegment [constr] StartX=-47.5 StartY=38.5 StartZ=0 EndX=-47.5 EndY=-38.5 EndZ=0
    g15: LineSegment [constr] StartX=-45.5 StartY=-40.5 StartZ=0 EndX=45.5 EndY=-40.5 EndZ=0
    g16: LineSegment [constr] StartX=47.5 StartY=-38.5 StartZ=0 EndX=47.5 EndY=38.5 EndZ=0
    g17: LineSegment [constr] StartX=45.5 StartY=40.5 StartZ=0 EndX=-45.5 EndY=40.5 EndZ=0
    g18: ArcOfCircle [constr] CenterX=-45.5 CenterY=38.5 CenterZ=0 NormalX=0 NormalY=0 NormalZ=1 AngleXU=0 Radius=2 StartAngle=1.5708 EndAngle=3.14159
    g19: ArcOfCircle [constr] CenterX=-45.5 CenterY=-38.5 CenterZ=0 NormalX=0 NormalY=0 NormalZ=1 AngleXU=0 Radius=2 StartAngle=3.14159 EndAngle=4.71239
    g20: ArcOfCircle [constr] CenterX=45.5 CenterY=-38.5 CenterZ=0 NormalX=0 NormalY=0 NormalZ=1 AngleXU=0 Radius=2 StartAngle=4.71239 EndAngle=6.28319
    g21: ArcOfCircle [constr] CenterX=45.5 CenterY=38.5 CenterZ=0 NormalX=0 NormalY=0 NormalZ=1 AngleXU=0 Radius=2 StartAngle=1.3e-15 EndAngle=1.5708
    g22: GeomPoint [constr] X=-47.5 Y=40.5 Z=0
    g23: GeomPoint [constr] X=47.5 Y=-40.5 Z=0
    g24: LineSegment [constr] StartX=-4.875 StartY=36 StartZ=0 EndX=-4.875 EndY=35.5 EndZ=0
    g25: LineSegment [constr] StartX=-3.375 StartY=34 StartZ=0 EndX=3.375 EndY=34 EndZ=0
    g26: LineSegment [constr] StartX=4.875 StartY=35.5 StartZ=0 EndX=4.875 EndY=36 EndZ=0
    g27: LineSegment [constr] StartX=3.375 StartY=37.5 StartZ=0 EndX=-3.375 EndY=37.5 EndZ=0
    g28: ArcOfCircle [constr] CenterX=-3.375 CenterY=36 CenterZ=0 NormalX=0 NormalY=0 NormalZ=1 AngleXU=0 Radius=1.5 StartAngle=1.5708 EndAngle=3.14159
    g29: ArcOfCircle [constr] CenterX=-3.375 CenterY=35.5 CenterZ=0 NormalX=0 NormalY=0 NormalZ=1 AngleXU=0 Radius=1.5 StartAngle=3.14159 EndAngle=4.71239
    g30: ArcOfCircle [constr] CenterX=3.375 CenterY=35.5 CenterZ=0 NormalX=0 NormalY=0 NormalZ=1 AngleXU=0 Radius=1.5 StartAngle=4.71239 EndAngle=6.28319
    g31: ArcOfCircle [constr] CenterX=3.375 CenterY=36 CenterZ=0 NormalX=0 NormalY=0 NormalZ=1 AngleXU=0 Radius=1.5 StartAngle=0 EndAngle=1.5708
    g32: GeomPoint [constr] X=-4.875 Y=37.5 Z=0
    g33: GeomPoint [constr] X=4.875 Y=34 Z=0
    g34: Circle [constr] CenterX=40.875 CenterY=34.375 CenterZ=0 NormalX=0 NormalY=0 NormalZ=1 AngleXU=0 Radius=1
    g35: Circle [constr] CenterX=-40.875 CenterY=34.375 CenterZ=0 NormalX=0 NormalY=0 NormalZ=1 AngleXU=0 Radius=1
    g36: Circle [constr] CenterX=-40.875 CenterY=-34.375 CenterZ=0 NormalX=0 NormalY=0 NormalZ=1 AngleXU=0 Radius=1
    g37: Circle [constr] CenterX=40.875 CenterY=-34.375 CenterZ=0 NormalX=0 NormalY=0 NormalZ=1 AngleXU=0 Radius=1
    g38: ArcOfCircle CenterX=40.875 CenterY=34.375 CenterZ=0 NormalX=0 NormalY=0 NormalZ=1 AngleXU=0 Radius=2.75 StartAngle=0 EndAngle=1.5708
    g39: ArcOfCircle CenterX=40.875 CenterY=-34.375 CenterZ=0 NormalX=0 NormalY=0 NormalZ=1 AngleXU=0 Radius=2.75 StartAngle=4.71239 EndAngle=6.28319
    g40: ArcOfCircle CenterX=-40.875 CenterY=-34.375 CenterZ=0 NormalX=0 NormalY=0 NormalZ=1 AngleXU=0 Radius=2.75 StartAngle=3.14159 EndAngle=4.71239
    g41: ArcOfCircle CenterX=-40.875 CenterY=34.375 CenterZ=0 NormalX=0 NormalY=0 NormalZ=1 AngleXU=0 Radius=2.75 StartAngle=1.5708 EndAngle=3.14159
    g42: LineSegment StartX=-43.625 StartY=34.375 StartZ=0 EndX=-43.625 EndY=-34.375 EndZ=0
    g43: LineSegment StartX=27.725 StartY=-37.125 StartZ=0 EndX=40.875 EndY=-37.125 EndZ=0
    g44: LineSegment StartX=43.625 StartY=-34.375 StartZ=0 EndX=43.625 EndY=34.375 EndZ=0
    g45: LineSegment StartX=-40.875 StartY=37.125 StartZ=0 EndX=-11.2375 EndY=37.125 EndZ=0
    g46: LineSegment StartX=40.875 StartY=37.125 StartZ=0 EndX=11.2375 EndY=37.125 EndZ=0
    g47: ArcOfCircle CenterX=11.2375 CenterY=33.9625 CenterZ=0 NormalX=0 NormalY=0 NormalZ=1 AngleXU=0 Radius=3.1625 StartAngle=1.5708 EndAngle=3.14159
    g48: ArcOfCircle CenterX=-11.2375 CenterY=33.9625 CenterZ=0 NormalX=0 NormalY=0 NormalZ=1 AngleXU=0 Radius=3.1625 StartAngle=0 EndAngle=1.5708
    g49: ArcOfCircle CenterX=-4.9125 CenterY=33.9625 CenterZ=0 NormalX=0 NormalY=0 NormalZ=1 AngleXU=0 Radius=3.1625 StartAngle=3.14159 EndAngle=4.71239
    g50: ArcOfCircle CenterX=4.9125 CenterY=33.9625 CenterZ=0 NormalX=0 NormalY=0 NormalZ=1 AngleXU=0 Radius=3.1625 StartAngle=4.71239 EndAngle=6.28319
    g51: LineSegment StartX=-4.9125 StartY=30.8 StartZ=0 EndX=4.9125 EndY=30.8 EndZ=0
    g52: LineSegment StartX=-6.125 StartY=2.875 StartZ=0 EndX=-6.125 EndY=-2.875 EndZ=0
    g53: LineSegment StartX=-2.875 StartY=-6.125 StartZ=0 EndX=2.875 EndY=-6.125 EndZ=0
    g54: LineSegment StartX=6.125 StartY=-2.875 StartZ=0 EndX=6.125 EndY=2.875 EndZ=0
    g55: LineSegment StartX=2.875 StartY=6.125 StartZ=0 EndX=-2.875 EndY=6.125 EndZ=0
    g56: ArcOfCircle CenterX=-2.875 CenterY=2.875 CenterZ=0 NormalX=0 NormalY=0 NormalZ=1 AngleXU=0 Radius=3.25 StartAngle=1.5708 EndAngle=3.14159
    g57: ArcOfCircle CenterX=-2.875 CenterY=-2.875 CenterZ=0 NormalX=0 NormalY=0 NormalZ=1 AngleXU=0 Radius=3.25 StartAngle=3.14159 EndAngle=4.71239
    g58: ArcOfCircle CenterX=2.875 CenterY=-2.875 CenterZ=0 NormalX=0 NormalY=0 NormalZ=1 AngleXU=0 Radius=3.25 StartAngle=4.71239 EndAngle=6.28319
    g59: ArcOfCircle CenterX=2.875 CenterY=2.875 CenterZ=0 NormalX=0 NormalY=0 NormalZ=1 AngleXU=0 Radius=3.25 StartAngle=0 EndAngle=1.5708
    g60: GeomPoint [constr] X=-6.125 Y=6.125 Z=0
    g61: GeomPoint [constr] X=6.125 Y=-6.125 Z=0
    g62: LineSegment StartX=-40.875 StartY=-37.125 StartZ=0 EndX=24.225 EndY=-37.125 EndZ=0
    g63: LineSegment StartX=24.225 StartY=-37.125 StartZ=0 EndX=24.225 EndY=-35.625 EndZ=0
    g64: LineSegment StartX=27.725 StartY=-37.125 StartZ=0 EndX=27.725 EndY=-35.625 EndZ=0
    g65: ArcOfCircle CenterX=25.975 CenterY=-35.625 CenterZ=0 NormalX=0 NormalY=0 NormalZ=1 AngleXU=0 Radius=1.75 StartAngle=0 EndAngle=3.14159
    g66: LineSegment StartX=39.451 StartY=18.1 StartZ=0 EndX=42.049 EndY=18.1 EndZ=0
    g67: LineSegment StartX=40.1005 StartY=21.475 StartZ=0 EndX=38.8014 EndY=19.225 EndZ=0
    g68: LineSegment StartX=41.3995 StartY=21.475 StartZ=0 EndX=42.6986 EndY=19.225 EndZ=0
    g69: ArcOfCircle CenterX=40.75 CenterY=21.1 CenterZ=0 NormalX=0 NormalY=0 NormalZ=1 AngleXU=0 Radius=0.75 StartAngle=0.523599 EndAngle=2.61799
    g70: ArcOfCircle CenterX=42.049 CenterY=18.85 CenterZ=0 NormalX=0 NormalY=0 NormalZ=1 AngleXU=0 Radius=0.75 StartAngle=4.71239 EndAngle=6.80678
    g71: ArcOfCircle CenterX=39.451 CenterY=18.85 CenterZ=0 NormalX=0 NormalY=0 NormalZ=1 AngleXU=0 Radius=0.75 StartAngle=2.61799 EndAngle=4.71239
    g72: LineSegment [constr] StartX=40.1005 StartY=21.475 StartZ=0 EndX=40.75 EndY=21.1 EndZ=0
    g73: LineSegment [constr] StartX=40.75 StartY=21.1 StartZ=0 EndX=41.3995 EndY=21.475 EndZ=0
    g74: LineSegment [constr] StartX=38.8014 StartY=19.225 StartZ=0 EndX=39.451 EndY=18.85 EndZ=0
    g75: LineSegment [constr] StartX=42.049 StartY=18.85 StartZ=0 EndX=42.6986 EndY=19.225 EndZ=0
    g76: LineSegment StartX=39.451 StartY=1.5 StartZ=0 EndX=42.049 EndY=1.5 EndZ=0
    g77: LineSegment StartX=38.8014 StartY=0.375 StartZ=0 EndX=40.1005 EndY=-1.875 EndZ=0
    g78: LineSegment StartX=42.6986 StartY=0.375 StartZ=0 EndX=41.3995 EndY=-1.875 EndZ=0
    g79: ArcOfCircle CenterX=39.451 CenterY=0.75 CenterZ=0 NormalX=0 NormalY=0 NormalZ=1 AngleXU=0 Radius=0.75 StartAngle=1.5708 EndAngle=3.66519
    g80: ArcOfCircle CenterX=42.049 CenterY=0.75 CenterZ=0 NormalX=0 NormalY=0 NormalZ=1 AngleXU=0 Radius=0.75 StartAngle=5.75959 EndAngle=7.85398
    g81: ArcOfCircle CenterX=40.75 CenterY=-1.5 CenterZ=0 NormalX=0 NormalY=0 NormalZ=1 AngleXU=0 Radius=0.75 StartAngle=3.66519 EndAngle=5.75959
    g82: LineSegment [constr] StartX=38.8014 StartY=0.375 StartZ=0 EndX=39.451 EndY=0.75 EndZ=0
    g83: LineSegment [constr] StartX=42.049 StartY=0.75 StartZ=0 EndX=42.6986 EndY=0.375 EndZ=0
    g84: LineSegment [constr] StartX=41.3995 StartY=-1.875 StartZ=0 EndX=40.75 EndY=-1.5 EndZ=0
    g85: LineSegment [constr] StartX=40.1005 StartY=-1.875 StartZ=0 EndX=40.75 EndY=-1.5 EndZ=0
    g86: LineSegment StartX=38.75 StartY=-18.35 StartZ=0 EndX=38.75 EndY=-20.85 EndZ=0
    g87: LineSegment StartX=39.5 StartY=-21.6 StartZ=0 EndX=42 EndY=-21.6 EndZ=0
    g88: LineSegment StartX=42.75 StartY=-20.85 StartZ=0 EndX=42.75 EndY=-18.35 EndZ=0
    g89: LineSegment StartX=42 StartY=-17.6 StartZ=0 EndX=39.5 EndY=-17.6 EndZ=0
    g90: ArcOfCircle CenterX=39.5 CenterY=-18.35 CenterZ=0 NormalX=0 NormalY=0 NormalZ=1 AngleXU=0 Radius=0.75 StartAngle=1.5708 EndAngle=3.14159
    g91: ArcOfCircle CenterX=39.5 CenterY=-20.85 CenterZ=0 NormalX=0 NormalY=0 NormalZ=1 AngleXU=0 Radius=0.75 StartAngle=3.14159 EndAngle=4.71239
    g92: ArcOfCircle CenterX=42 CenterY=-20.85 CenterZ=0 NormalX=0 NormalY=0 NormalZ=1 AngleXU=0 Radius=0.75 StartAngle=4.71239 EndAngle=6.28319
    g93: ArcOfCircle CenterX=42 CenterY=-18.35 CenterZ=0 NormalX=0 NormalY=0 NormalZ=1 AngleXU=0 Radius=0.75 StartAngle=1.6e-15 EndAngle=1.5708
    g94: GeomPoint [constr] X=38.75 Y=-17.6 Z=0
    g95: GeomPoint [constr] X=42.75 Y=-21.6 Z=0
    g96: Circle CenterX=12.5 CenterY=17.125 CenterZ=0 NormalX=0 NormalY=0 NormalZ=1 AngleXU=0 Radius=4.5
    g97: Circle CenterX=-12.5 CenterY=17.125 CenterZ=0 NormalX=0 NormalY=0 NormalZ=1 AngleXU=0 Radius=4.5
    g98: GeomPoint X=40.75 Y=1.5 Z=0
    g99: GeomPoint X=40.75 Y=18.1 Z=0
    g100: GeomPoint X=-12.5 Y=17.125 Z=0
    g101: GeomPoint X=12.5 Y=17.125 Z=0
  constraints (262):
    c: Tangent(g0,g4) = -1.5708
    c: Tangent(g0,g5) = -1.5708
    c: Tangent(g1,g5) = -1.5708
    c: Tangent(g1,g6) = -1.5708
    c: Tangent(g2,g6) = -1.5708
    c: Tangent(g2,g7) = -1.5708
    c: Tangent(g3,g7) = -1.5708
    c: Tangent(g3,g4) = -1.5708
    c: Horizontal(g0)
    c: Horizontal(g2)
    c: Vertical(g1)
    c: Vertical(g3)
    c: Equal(g4,g5)
    c: Equal(g5,g6)
    c: Equal(g6,g7)
    c: PointOnObject(g8,g0)
    c: PointOnObject(g8,g3)
    c: PointOnObject(g9,g1)
    c: PointOnObject(g9,g2)
    c: Radius(g5) = 1.25
    c: Distance(g2,g0) = 8.25
    c: Equal(g0,g1)
    c: Symmetric(g8,g9,g-1)
    c: Diameter(g12) = 3
    c: Vertical(g12,g10)
    c: Equal(g11,g10)
    c: Equal(g10,g12)
    c: DistanceX(g-1,g11) = 40.75
    c: Diameter(g13) = 3
    c: DistanceX(g13,g-1) = 19
    c: Tangent(g14,g18) = -1.5708
    c: Tangent(g14,g19) = -1.5708
    c: Tangent(g15,g19) = -1.5708
    c: Tangent(g15,g20) = -1.5708
    c: Tangent(g16,g20) = -1.5708
    c: Tangent(g17,g18) = -1.5708
    c: Vertical(g14)
    c: Horizontal(g15)
    c: Horizontal(g17)
    c: Equal(g18,g19)
    c: Equal(g19,g20)
    c: Equal(g20,g21)
    c: PointOnObject(g22,g14)
    c: PointOnObject(g22,g17)
    c: PointOnObject(g23,g15)
    c: PointOnObject(g23,g16)
    c: Distance(g16,g14) = 95
    c: Distance(g15,g17) = 81
    c: Symmetric(g22,g23,g-1)
    c: Tangent(g24,g28) = -1.5708
    c: Tangent(g24,g29) = -1.5708
    c: Tangent(g25,g29) = -1.5708
    c: Tangent(g25,g30) = -1.5708
    c: Tangent(g26,g30) = -1.5708
    c: Tangent(g26,g31) = -1.5708
    c: Tangent(g27,g31) = -1.5708
    c: Tangent(g27,g28) = -1.5708
    c: Vertical(g24)
    c: Vertical(g26)
    c: Horizontal(g25)
    c: Equal(g28,g29)
    c: Equal(g29,g30)
    c: Equal(g30,g31)
    c: PointOnObject(g32,g24)
    c: PointOnObject(g32,g27)
    c: PointOnObject(g33,g25)
    c: PointOnObject(g33,g26)
    c: Radius(g29) = 1.5
    c: Distance(g26,g24) = 9.75
    c: Distance(g25,g27) = 3.5
    c: Symmetric(g27,g27,g-2)
    c: Distance(g-1,g25) = 34
    c: Diameter(g34) = 2
    c: Diameter(g35) = 2
    c: Diameter(g36) = 2
    c: Diameter(g37) = 2
    c: Horizontal(g37,g36)
    c: Horizontal(g34,g35)
    c: Vertical(g34,g37)
    c: Vertical(g35,g36)
    c: Symmetric(g36,g34,g-1)
    c: DistanceX(g35,g34) = 81.75
    c: Distance(g37,g34) = 68.75
    c: Coincident(g38,g34)
    c: Coincident(g39,g37)
    c: Radius(g40) = 2.75
    c: Coincident(g40,g36)
    c: Coincident(g41,g35)
    c: Equal(g41,g40)
    c: Equal(g40,g39)
    c: Equal(g39,g38)
    c: Horizontal(g43)
    c: Horizontal(g45)
    c: Horizontal(g46)
    c: Coincident(g47,g46)
    c: Coincident(g48,g45)
    c: Vertical(g48,g45)
    c: Horizontal(g48,g48)
    c: Coincident(g49,g48)
    c: Coincident(g50,g47)
    c: Vertical(g50,g50)
    c: Horizontal(g50,g47)
    c: Equal(g50,g47)
    c: Horizontal(g47,g47)
    c: Vertical(g46,g47)
    c: Horizontal(g48,g49)
    c: Vertical(g49,g49)
    c: Equal(g48,g49)
    c: Coincident(g51,g49)
    c: Coincident(g51,g50)
    c: Distance(g25,g51) = 3.2
    c: Symmetric(g49,g50,g-2)
    c: DistanceX(g26,g47) = 3.2
    c: Vertical(g41,g35)
    c: Horizontal(g38,g34)
    c: Vertical(g39,g37)
    c: Radius(g20) = 2
    c: Tangent(g52,g56) = -1.5708
    c: Tangent(g52,g57) = -1.5708
    c: Tangent(g53,g57) = -1.5708
    c: Tangent(g53,g58) = -1.5708
    c: Tangent(g54,g58) = -1.5708
    c: Tangent(g54,g59) = -1.5708
    c: Tangent(g55,g59) = -1.5708
    c: Tangent(g55,g56) = -1.5708
    c: Vertical(g52)
    c: Vertical(g54)
    c: Horizontal(g53)
    c: Horizontal(g55)
    c: Equal(g56,g57)
    c: Equal(g57,g58)
    c: Equal(g58,g59)
    c: PointOnObject(g60,g52)
    c: PointOnObject(g60,g55)
    c: PointOnObject(g61,g53)
    c: PointOnObject(g61,g54)
    c: Coincident(g58,g7)
    c: Coincident(g56,g5)
    c: Distance(g55,g0) = 2
    c: Vertical(g40,g36)
    c: Coincident(g40,g42)
    c: Tangent(g62,g40) = -1.5708
    c: Coincident(g63,g62)
    c: Vertical(g63)
    c: Coincident(g64,g43)
    c: Vertical(g64)
    c: Coincident(g65,g63)
    c: Coincident(g65,g64)
    c: Horizontal(g64,g65)
    c: Horizontal(g65,g63)
    c: Coincident(g43,g39)
    c: Coincident(g39,g44)
    c: Coincident(g38,g44)
    c: Vertical(g38,g34)
    c: Coincident(g46,g38)
    c: Coincident(g45,g41)
    c: Coincident(g42,g41)
    c: Horizontal(g41,g35)
    c: DistanceX(g43,g43) = 13.15
    c: Radius(g65) = 1.75
    c: DistanceY(g64,g64) = 1.5
    c: Horizontal(g40,g36)
    c: Horizontal(g37,g39)
    c: Coincident(g21,g16)
    c: Horizontal(g21,g16)
    c: Coincident(g17,g21)
    c: Vertical(g21,g17)
    c: Vertical(g16)
    c: Symmetric(g97,g96,g-2)
    c: Distance(g96,g0) = 13
    c: Horizontal(g13,g-1)
    c: Horizontal(g66)
    c: Coincident(g69,g67)
    c: Coincident(g69,g68)
    c: Coincident(g70,g66)
    c: Coincident(g70,g68)
    c: Coincident(g71,g66)
    c: Coincident(g71,g67)
    c: Equal(g69,g71)
    c: Equal(g71,g70)
    c: Vertical(g66,g71)
    c: Vertical(g66,g70)
    c: PointOnObject(g71,g12)
    c: PointOnObject(g70,g12)
    c: Equal(g66,g67)
    c: Equal(g67,g68)
    c: Coincident(g72,g67)
    c: Coincident(g72,g69)
    c: Coincident(g73,g69)
    c: Coincident(g73,g68)
    c: PointOnObject(g69,g12)
    c: Perpendicular(g68,g73)
    c: Perpendicular(g67,g72)
    c: Coincident(g74,g67)
    c: Coincident(g74,g71)
    c: Coincident(g75,g70)
    c: Coincident(g75,g68)
    c: Perpendicular(g68,g75)
    c: Perpendicular(g67,g74)
    c: Horizontal(g76)
    c: Coincident(g79,g77)
    c: Coincident(g79,g76)
    c: Coincident(g80,g76)
    c: Coincident(g80,g78)
    c: Coincident(g81,g77)
    c: Coincident(g81,g78)
    c: Vertical(g79,g76)
    c: Vertical(g80,g76)
    c: PointOnObject(g79,g10)
    c: PointOnObject(g80,g10)
    c: PointOnObject(g81,g10)
    c: Equal(g80,g79)
    c: Equal(g79,g81)
    c: Equal(g78,g76)
    c: Equal(g76,g77)
    c: Coincident(g82,g77)
    c: Coincident(g82,g79)
    c: Coincident(g83,g80)
    c: Coincident(g83,g78)
    c: Coincident(g84,g78)
    c: Coincident(g84,g81)
    c: Coincident(g85,g77)
    c: Coincident(g85,g81)
    c: Perpendicular(g85,g77)
    c: Perpendicular(g77,g82)
    c: Perpendicular(g78,g84)
    c: Perpendicular(g78,g83)
    c: Tangent(g86,g90) = -1.5708
    c: Tangent(g86,g91) = -1.5708
    c: Tangent(g87,g91) = -1.5708
    c: Tangent(g87,g92) = -1.5708
    c: Tangent(g88,g92) = -1.5708
    c: Tangent(g88,g93) = -1.5708
    c: Tangent(g89,g93) = -1.5708
    c: Tangent(g89,g90) = -1.5708
    c: Vertical(g86)
    c: Vertical(g88)
    c: Horizontal(g87)
    c: Horizontal(g89)
    c: Equal(g90,g91)
    c: Equal(g91,g92)
    c: Equal(g92,g93)
    c: PointOnObject(g94,g86)
    c: PointOnObject(g94,g89)
    c: PointOnObject(g95,g87)
    c: PointOnObject(g95,g88)
    c: Distance(g86,g88) = 4
    c: Equal(g92,g80)
    c: Equal(g86,g89)
    c: Diameter(g97) = 9
    c: Equal(g97,g96)
    c: PointOnObject(g10,g-1)
    c: Symmetric(g91,g93,g11)
    c: Distance(g12,g-1) = 19.6
    c: Symmetric(g12,g11,g10)
    c: Symmetric(g76,g76,g98)
    c: PointOnObject(g98,g10)
    c: Symmetric(g66,g66,g99)
    c: PointOnObject(g99,g12)
    c: DistanceX(g97,g96) = 25
    c: Coincident(g100,g97)
    c: Coincident(g101,g96)
FEATURE [PartDesign::Pad] Pad
  Direction = (0,-1,2e-16)
  Length = 2
  Length2 = 10
  Placement = pos=(0,0,0) rot=(1,0,0;1.5708rad)
  Profile = -> Sketch039 [Edge3,Edge2,Edge1,Edge8,Edge7,Edge6,Edge5,Edge4,Edge9,Edge24,Edge23,Edge22,Edge21,Edge20,Edge19,Edge18,Edge17,Edge16,Edge15,Edge14,Edge13,Edge12,Edge11,Edge10,Edge27,Edge26,Edge25,Edge37,Edge36,Edge41,Edge40,Vertex59,Edge39,Edge38,Edge43,Edge42,Edge47,Edge46,Edge45,Edge44,+8 more]
  ReferenceAxis = -> Sketch039 [N_Axis]
  Refine = true
  SideType = 0
  Suppressed = false
  Type = 0
  Type2 = 0
FEATURE [PartDesign::Pad] Pad027
  BaseFeature = -> Pad
  Direction = (0,-1,2e-16)
  Length = 5
  Length2 = 10
  Placement = pos=(0,0,0) rot=(1,0,0;1.5708rad)
  Profile = -> Sketch039 [Edge33,Edge34,Edge35,Edge28,Edge29,Edge30,Edge31,Edge32,Edge7,Edge8,Edge1,Edge2,Edge3,Edge4,Edge5,Edge6]
  ReferenceAxis = -> Sketch039 [N_Axis]
  Refine = true
  SideType = 0
  Suppressed = false
  Type = 0
  Type2 = 0
FEATURE [Sketcher::SketchObject] Sketch040
  ArcFitTolerance = 1e-06
  AttachmentSupport = -> [Pad]
  ExternalTypes = [0]
  FullyConstrained = true
  MakeInternals = false
  MapMode = 5
  Placement = pos=(-2.82e-14,-1.63e-14,-37.125) rot=(1,0,0;3.14159rad)
  _ExternalGeoVersion = 0
  sketch-geometry (8):
    g0: LineSegment StartX=-28.25 StartY=1 StartZ=0 EndX=11.75 EndY=1 EndZ=0
    g1: LineSegment StartX=11.75 StartY=1 StartZ=0 EndX=11.75 EndY=1.5 EndZ=0
    g2: LineSegment StartX=11.75 StartY=1.5 StartZ=0 EndX=-28.25 EndY=1.5 EndZ=0
    g3: LineSegment StartX=-28.25 StartY=1.5 StartZ=0 EndX=-28.25 EndY=1 EndZ=0
    g4: LineSegment StartX=30.25 StartY=1.5 StartZ=0 EndX=38.25 EndY=1.5 EndZ=0
    g5: LineSegment StartX=38.25 StartY=1.5 StartZ=0 EndX=38.25 EndY=1 EndZ=0
    g6: LineSegment StartX=38.25 StartY=1 StartZ=0 EndX=30.25 EndY=1 EndZ=0
    g7: LineSegment StartX=30.25 StartY=1 StartZ=0 EndX=30.25 EndY=1.5 EndZ=0
  constraints (24):
    c: Coincident(g0,g1)
    c: Coincident(g1,g2)
    c: Coincident(g2,g3)
    c: Coincident(g3,g0)
    c: Horizontal(g0)
    c: Horizontal(g2)
    c: Vertical(g1)
    c: Vertical(g3)
    c: Distance(g1,g3) = 40
    c: Distance(g0,g2) = 0.5
    c: Coincident(g4,g5)
    c: Coincident(g5,g6)
    c: Coincident(g6,g7)
    c: Coincident(g7,g4)
    c: Horizontal(g4)
    c: Horizontal(g6)
    c: Vertical(g5)
    c: Vertical(g7)
    c: Distance(g5,g7) = 8
    c: Distance(g4,g6) = 0.5
    c: Distance(g7,g1) = 18.5
    c: Distance(g-1,g0) = 1
    c: Distance(g-2,g1) = 11.75
    c: Horizontal(g0,g6)
FEATURE [PartDesign::Revolution] Revolution007
  Angle = 360
  Angle2 = 60
  Axis = (1,0,0)
  Base = (-28.25,-1,-37.125)
  BaseFeature = -> Pad027
  FuseOrder = 1
  Placement = pos=(0,0,0) rot=(1,0,0;1.5708rad)
  Profile = -> Sketch040
  ReferenceAxis = -> Sketch040 [Edge1]
  Refine = true
  Suppressed = false
  Type = 0
FEATURE [Sketcher::SketchObject] Sketch041
  ArcFitTolerance = 1e-06
  AttachmentSupport = -> [Pad]
  ExternalTypes = [0]
  FullyConstrained = true
  MakeInternals = false
  MapMode = 5
  Placement = pos=(43.625,0,0) rot=(0.707107,0,0.707107;3.14159rad)
  _ExternalGeoVersion = 0
  sketch-geometry (4):
    g0: LineSegment StartX=-20 StartY=1 StartZ=0 EndX=20 EndY=1 EndZ=0
    g1: LineSegment StartX=20 StartY=1 StartZ=0 EndX=20 EndY=1.5 EndZ=0
    g2: LineSegment StartX=20 StartY=1.5 StartZ=0 EndX=-20 EndY=1.5 EndZ=0
    g3: LineSegment StartX=-20 StartY=1.5 StartZ=0 EndX=-20 EndY=1 EndZ=0
  constraints (11):
    c: Coincident(g0,g1)
    c: Coincident(g1,g2)
    c: Coincident(g2,g3)
    c: Coincident(g3,g0)
    c: Horizontal(g0)
    c: Vertical(g1)
    c: Vertical(g3)
    c: Distance(g1,g3) = 40
    c: Distance(g0,g2) = 0.5
    c: Symmetric(g1,g2,g-2)
    c: Distance(g-1,g0) = 1
FEATURE [PartDesign::Revolution] Revolution008
  Angle = 360
  Angle2 = 60
  Axis = (2e-16,0,1)
  Base = (43.625,-1,-20)
  BaseFeature = -> Revolution007
  FuseOrder = 1
  Placement = pos=(0,0,0) rot=(1,0,0;1.5708rad)
  Profile = -> Sketch041
  ReferenceAxis = -> Sketch041 [Edge1]
  Refine = true
  Suppressed = false
  Type = 0
FEATURE [PartDesign::Mirrored] Mirrored003
  BaseFeature = -> Revolution008
  MirrorPlane = -> YZ_Plane009
  Originals = -> [Revolution008]
  Placement = pos=(0,0,0) rot=(1,0,0;1.5708rad)
  Refine = true
  Suppressed = false
  TransformMode = 0
FEATURE [Sketcher::SketchObject] Sketch042
  ArcFitTolerance = 1e-06
  AttachmentSupport = -> [Pad]
  ExternalTypes = [0]
  FullyConstrained = true
  MakeInternals = false
  MapMode = 5
  Placement = pos=(0,1.63e-14,37.125) rot=(0,0,1;3.14159rad)
  _ExternalGeoVersion = 0
  sketch-geometry (8):
    g0: LineSegment StartX=-31.75 StartY=0.9 StartZ=0 EndX=-31.75 EndY=0.5 EndZ=0
    g1: LineSegment StartX=-31.75 StartY=0.5 StartZ=0 EndX=-16.75 EndY=0.5 EndZ=0
    g2: LineSegment StartX=-16.75 StartY=0.5 StartZ=0 EndX=-16.75 EndY=0.9 EndZ=0
    g3: LineSegment StartX=-16.75 StartY=0.9 StartZ=0 EndX=-31.75 EndY=0.9 EndZ=0
    g4: LineSegment StartX=16.75 StartY=1 StartZ=0 EndX=16.75 EndY=0.5 EndZ=0
    g5: LineSegment StartX=16.75 StartY=0.5 StartZ=0 EndX=31.75 EndY=0.5 EndZ=0
    g6: LineSegment StartX=31.75 StartY=0.5 StartZ=0 EndX=31.75 EndY=1 EndZ=0
    g7: LineSegment StartX=31.75 StartY=1 StartZ=0 EndX=16.75 EndY=1 EndZ=0
  constraints (23):
    c: Coincident(g0,g1)
    c: Coincident(g1,g2)
    c: Coincident(g2,g3)
    c: Coincident(g3,g0)
    c: Vertical(g0)
    c: Vertical(g2)
    c: Horizontal(g1)
    c: Horizontal(g3)
    c: Distance(g0,g2) = 15
    c: Distance(g1,g3) = 0.4
    c: Coincident(g4,g5)
    c: Coincident(g5,g6)
    c: Coincident(g6,g7)
    c: Coincident(g7,g4)
    c: Vertical(g4)
    c: Vertical(g6)
    c: Horizontal(g5)
    c: Horizontal(g7)
    c: Distance(g5,g7) = 0.5
    c: Symmetric(g5,g0,g-2)
    c: Distance(g4,g2) = 33.5
    c: Distance(g-1,g1) = 0.5
    c: Equal(g7,g3)
FEATURE [PartDesign::Revolution] Revolution009
  Angle = 360
  Angle2 = 60
  Axis = (1,0,0)
  Base = (-31.75,-1,37.125)
  BaseFeature = -> Mirrored003
  FuseOrder = 1
  Placement = pos=(0,0,0) rot=(1,0,0;1.5708rad)
  Profile = -> Sketch042
  ReferenceAxis = -> Sketch042 [Edge8]
  Refine = true
  Reversed = true
  Suppressed = false
  Type = 0
FEATURE [Sketcher::SketchObject] Sketch043
  ArcFitTolerance = 1e-06
  AttachmentSupport = -> [Pad]
  ExternalTypes = [0]
  FullyConstrained = true
  MakeInternals = false
  MapMode = 5
  Placement = pos=(0,-2,0) rot=(1,0,0;1.5708rad)
  _ExternalGeoVersion = 0
  sketch-geometry (24):
    g0: LineSegment StartX=-42.75 StartY=32.5 StartZ=0 EndX=-42.75 EndY=-32.5 EndZ=0
    g1: LineSegment StartX=-42.75 StartY=-32.5 StartZ=0 EndX=-42.25 EndY=-32.5 EndZ=0
    g2: LineSegment StartX=-42.25 StartY=-32.5 StartZ=0 EndX=-42.25 EndY=32.5 EndZ=0
    g3: LineSegment StartX=-42.25 StartY=32.5 StartZ=0 EndX=-42.75 EndY=32.5 EndZ=0
    g4: LineSegment StartX=-40.5 StartY=-36.25 StartZ=0 EndX=22.5 EndY=-36.25 EndZ=0
    g5: LineSegment StartX=22.5 StartY=-36.25 StartZ=0 EndX=22.5 EndY=-35.75 EndZ=0
    g6: LineSegment StartX=22.5 StartY=-35.75 StartZ=0 EndX=-40.5 EndY=-35.75 EndZ=0
    g7: LineSegment StartX=-40.5 StartY=-35.75 StartZ=0 EndX=-40.5 EndY=-36.25 EndZ=0
    g8: LineSegment StartX=28.5 StartY=-36.25 StartZ=0 EndX=40.5 EndY=-36.25 EndZ=0
    g9: LineSegment StartX=40.5 StartY=-36.25 StartZ=0 EndX=40.5 EndY=-35.75 EndZ=0
    g10: LineSegment StartX=40.5 StartY=-35.75 StartZ=0 EndX=28.5 EndY=-35.75 EndZ=0
    g11: LineSegment StartX=28.5 StartY=-35.75 StartZ=0 EndX=28.5 EndY=-36.25 EndZ=0
    g12: LineSegment StartX=12.25 StartY=36.25 StartZ=0 EndX=12.25 EndY=35.75 EndZ=0
    g13: LineSegment StartX=12.25 StartY=35.75 StartZ=0 EndX=39.25 EndY=35.75 EndZ=0
    g14: LineSegment StartX=39.25 StartY=35.75 StartZ=0 EndX=39.25 EndY=36.25 EndZ=0
    g15: LineSegment StartX=39.25 StartY=36.25 StartZ=0 EndX=12.25 EndY=36.25 EndZ=0
    g16: LineSegment StartX=-39.25 StartY=36.25 StartZ=0 EndX=-39.25 EndY=35.75 EndZ=0
    g17: LineSegment StartX=-39.25 StartY=35.75 StartZ=0 EndX=-12.25 EndY=35.75 EndZ=0
    g18: LineSegment StartX=-12.25 StartY=35.75 StartZ=0 EndX=-12.25 EndY=36.25 EndZ=0
    g19: LineSegment StartX=-12.25 StartY=36.25 StartZ=0 EndX=-39.25 EndY=36.25 EndZ=0
    g20: LineSegment [constr] StartX=28.5 StartY=-36.25 StartZ=0 EndX=22.5 EndY=-36.25 EndZ=0
    g21: LineSegment [constr] StartX=28.5 StartY=-35.75 StartZ=0 EndX=22.5 EndY=-35.75 EndZ=0
    g22: LineSegment [constr] StartX=-12.25 StartY=35.75 StartZ=0 EndX=12.25 EndY=35.75 EndZ=0
    g23: LineSegment [constr] StartX=12.25 StartY=36.25 StartZ=0 EndX=-12.25 EndY=36.25 EndZ=0
  constraints (65):
    c: Coincident(g0,g1)
    c: Coincident(g1,g2)
    c: Coincident(g2,g3)
    c: Coincident(g3,g0)
    c: Vertical(g0)
    c: Horizontal(g1)
    c: Horizontal(g3)
    c: Coincident(g4,g5)
    c: Coincident(g5,g6)
    c: Coincident(g6,g7)
    c: Coincident(g7,g4)
    c: Horizontal(g4)
    c: Horizontal(g6)
    c: Vertical(g5)
    c: Vertical(g7)
    c: Coincident(g8,g9)
    c: Coincident(g9,g10)
    c: Coincident(g10,g11)
    c: Coincident(g11,g8)
    c: Horizontal(g8)
    c: Horizontal(g10)
    c: Vertical(g9)
    c: Vertical(g11)
    c: Coincident(g12,g13)
    c: Coincident(g13,g14)
    c: Coincident(g14,g15)
    c: Coincident(g15,g12)
    c: Vertical(g12)
    c: Vertical(g14)
    c: Horizontal(g13)
    c: Horizontal(g15)
    c: Coincident(g16,g17)
    c: Coincident(g17,g18)
    c: Coincident(g18,g19)
    c: Coincident(g19,g16)
    c: Vertical(g16)
    c: Vertical(g18)
    c: Horizontal(g17)
    c: Horizontal(g19)
    c: Equal(g18,g14)
    c: Equal(g3,g14)
    c: Equal(g5,g14)
    c: Equal(g9,g14)
    c: Coincident(g20,g8)
    c: Coincident(g20,g4)
    c: Coincident(g21,g10)
    c: Coincident(g21,g5)
    c: DistanceY(g14,g14) = 0.5
    c: Coincident(g22,g17)
    c: Coincident(g22,g12)
    c: Coincident(g23,g12)
    c: Coincident(g23,g18)
    c: Equal(g15,g19)
    c: Symmetric(g16,g14,g-2)
    c: DistanceX(g10,g10) = 12
    c: DistanceX(g21,g21) = 6
    c: DistanceX(g6,g6) = 63
    c: Symmetric(g6,g9,g-2)
    c: Distance(g-2,g2) = 42.25
    c: Symmetric(g2,g1,g-1)
    c: DistanceY(g0,g0) = 65
    c: DistanceX(g19,g19) = 27
    c: DistanceX(g23,g23) = 24.5
    c: Distance(g-1,g17) = 35.75
    c: Distance(g-1,g6) = 35.75
FEATURE [PartDesign::Pocket] Pocket005
  BaseFeature = -> Revolution009
  Direction = (0,1,-2e-16)
  Length = 1.5
  Length2 = 5
  Placement = pos=(0,0,0) rot=(1,0,0;1.5708rad)
  Profile = -> Sketch043
  ReferenceAxis = -> Sketch043 [N_Axis]
  Refine = true
  SideType = 0
  Suppressed = false
  Type = 0
  Type2 = 0
FEATURE [PartDesign::Pad] Pad028
  BaseFeature = -> Pocket005
  Direction = (0,-1,0)
  Length = 5
  Length2 = 10
  Placement = pos=(0,0,0) rot=(1,0,0;1.5708rad)
  Profile = -> Sketch039 [Edge57,Edge56]
  ReferenceAxis = -> Sketch039 [N_Axis]
  Refine = true
  SideType = 0
  Suppressed = false
  Type = 0
  Type2 = 0
FEATURE [PartDesign::Hole] Hole
  BaseFeature = -> Pad028
  BaseProfileType = 7
  CustomThreadClearance = 0
  Depth = 25
  DepthType = 0
  Diameter = 5.026
  DrillForDepth = false
  DrillPoint = 1
  DrillPointAngle = 118
  HoleCutCountersinkAngle = 90
  HoleCutCustomValues = false
  HoleCutDepth = 3.4
  HoleCutDiameter = 6.8
  HoleCutType = 2
  ModelThread = true
  Placement = pos=(0,0,0) rot=(1,0,0;1.5708rad)
  Profile = -> Sketch039 [Vertex60,Vertex61]
  Refine = true
  Reversed = true
  Suppressed = false
  Tapered = false
  TaperedAngle = 90
  ThreadClass = 0
  ThreadDepth = 25
  ThreadDepthType = 0
  ThreadDiameter = 6
  ThreadDirection = 0
  ThreadFit = 0
  ThreadSize = 14
  ThreadType = 1
  Threaded = true
  UseCustomThreadClearance = false
FEATURE [PartDesign::Body] Body009  label="Back"
  AllowCompound = true
  Group = -> [Pad,Sketch039,Pad027,Sketch040,Revolution007,Sketch041,Revolution008,Mirrored003,Sketch042,Revolution009,Sketch043,Pocket005,Pad028,Hole]
  Origin = -> Origin018
  Placement = pos=(0,7.5,0) rot=(0,0,1;0rad)
  Tip = -> Hole
